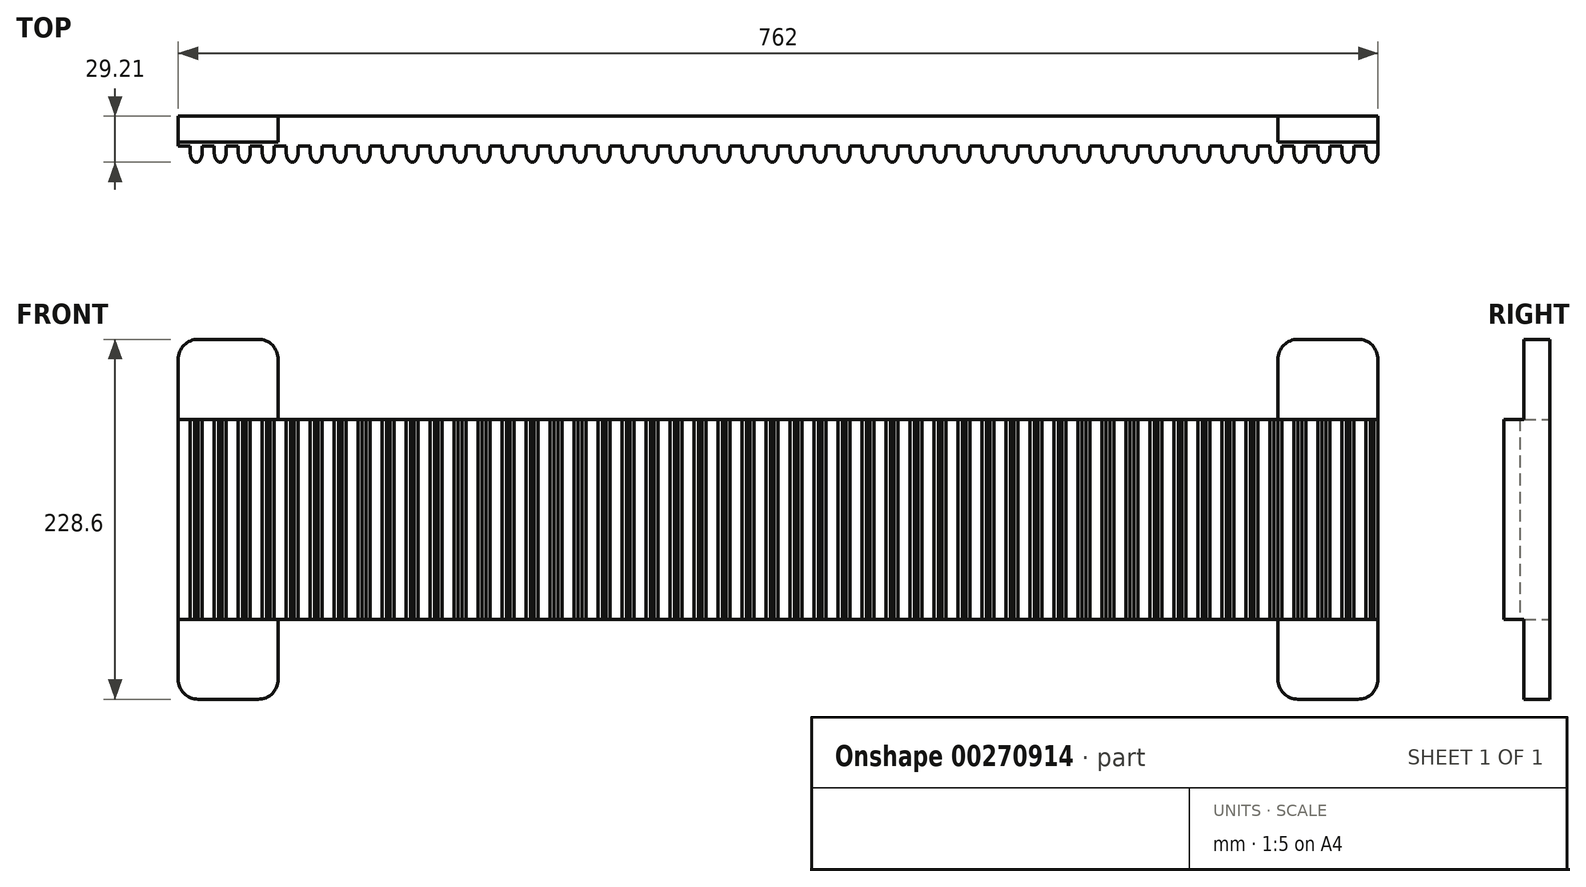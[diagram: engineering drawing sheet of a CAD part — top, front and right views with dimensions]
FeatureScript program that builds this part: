
annotation { "Feature Type Name" : "Feature", "Feature Type Description" : "" }
export const myFeature = defineFeature(function(context is Context, id is Id, definition is map)
    precondition{}
    {
        {
            var Q0;
            Q0=qCreatedBy(makeId("Front.planeOp"),FACE);
            var sketch = newSketch(context, id + "F0", { "sketchPlane" : qUnion([Q0])});
            skLineSegment(sketch, "E0", {"start": v(0, 0) * mm, "end": v(63.5, 0) * mm});
            skLineSegment(sketch, "E1.0", {"start": v(0, 228.6) * mm, "end": v(63.5, 228.6) * mm});
            skLineSegment(sketch, "E2", {"start": v(762, 0) * mm, "end": v(762, 228.6) * mm});
            skLineSegment(sketch, "E3", {"start": v(0, 228.6) * mm, "end": v(0, 0) * mm});
            skLineSegment(sketch, "E4.0", {"start": v(63.5, 177.8) * mm, "end": v(698.5, 177.8) * mm});
            skLineSegment(sketch, "E5.0", {"start": v(63.5, 50.8) * mm, "end": v(698.5, 50.8) * mm});
            skLineSegment(sketch, "E6.0", {"start": v(63.5, 228.6) * mm, "end": v(63.5, 177.8) * mm});
            skLineSegment(sketch, "E7.0", {"start": v(698.5, 0) * mm, "end": v(698.5, 50.8) * mm});
            skLineSegment(sketch, "E8.trimOffspring", {"start": v(698.5, 228.6) * mm, "end": v(762, 228.6) * mm});
            skLineSegment(sketch, "E9.trimOffspring", {"start": v(698.5, 0) * mm, "end": v(762, 0) * mm});
            skLineSegment(sketch, "E10.trimOffspring", {"start": v(698.5, 177.8) * mm, "end": v(698.5, 228.6) * mm});
            skLineSegment(sketch, "E11.trimOffspring", {"start": v(63.5, 50.8) * mm, "end": v(63.5, 0) * mm});
            skSolve(sketch);
        }
        {
            var Q0;
            Q0 = qSketchRegion(id + "F0", true);
            extrude(context, id + "F1", {"entities" : qUnion([Q0]), "depth" : 19.05 * mm});
        }
        {
            var Q0;
            Q0=makeQuery(id+"F1.opExtrude","CAP_FACE",FACE,{"disambiguationData":[OSD([sQuery(id+"F0.wireOp",EDGE,"E0"),sQuery(id+"F0.wireOp",EDGE,"E1.0"),sQuery(id+"F0.wireOp",EDGE,"E2"),sQuery(id+"F0.wireOp",EDGE,"E3"),sQuery(id+"F0.wireOp",EDGE,"E4.0"),sQuery(id+"F0.wireOp",EDGE,"E5.0"),sQuery(id+"F0.wireOp",EDGE,"E6.0"),sQuery(id+"F0.wireOp",EDGE,"E7.0"),sQuery(id+"F0.wireOp",EDGE,"E8.trimOffspring"),sQuery(id+"F0.wireOp",EDGE,"E9.trimOffspring"),sQuery(id+"F0.wireOp",EDGE,"E10.trimOffspring"),sQuery(id+"F0.wireOp",EDGE,"E11.trimOffspring")])],"isStart":false});
            var sketch = newSketch(context, id + "F2", { "sketchPlane" : qUnion([Q0])});
            skLineSegment(sketch, "E12", {"start": v(762, 177.8) * mm, "end": v(0, 177.8) * mm});
            skLineSegment(sketch, "E13", {"start": v(0, 177.8) * mm, "end": v(0, 50.8) * mm});
            skLineSegment(sketch, "E14", {"start": v(0, 50.8) * mm, "end": v(762, 50.8) * mm});
            skLineSegment(sketch, "E15", {"start": v(762, 50.8) * mm, "end": v(762, 177.8) * mm});
            skLineSegment(sketch, "E16.1.0.0", {"start": v(7.62, 177.8) * mm, "end": v(7.62, 50.8) * mm});
            skLineSegment(sketch, "E16.2.0.0", {"start": v(15.24, 177.8) * mm, "end": v(15.24, 50.8) * mm});
            skLineSegment(sketch, "E16.direction1", {"start": v(0, 50.8) * mm, "end": v(7.62, 50.8) * mm, "construction": true});
            skLineSegment(sketch, "E17.0.3.0", {"start": v(22.86, 177.8) * mm, "end": v(22.86, 50.8) * mm});
            skLineSegment(sketch, "E17.0.4.0", {"start": v(30.48, 177.8) * mm, "end": v(30.48, 50.8) * mm});
            skLineSegment(sketch, "E17.0.5.0", {"start": v(38.1, 177.8) * mm, "end": v(38.1, 50.8) * mm});
            skLineSegment(sketch, "E17.0.6.0", {"start": v(45.72, 177.8) * mm, "end": v(45.72, 50.8) * mm});
            skLineSegment(sketch, "E17.0.7.0", {"start": v(53.34, 177.8) * mm, "end": v(53.34, 50.8) * mm});
            skLineSegment(sketch, "E17.0.8.0", {"start": v(60.96, 177.8) * mm, "end": v(60.96, 50.8) * mm});
            skLineSegment(sketch, "E17.0.9.0", {"start": v(68.58, 177.8) * mm, "end": v(68.58, 50.8) * mm});
            skLineSegment(sketch, "E17.0.10.0", {"start": v(76.2, 177.8) * mm, "end": v(76.2, 50.8) * mm});
            skLineSegment(sketch, "E17.0.11.0", {"start": v(83.82, 177.8) * mm, "end": v(83.82, 50.8) * mm});
            skLineSegment(sketch, "E17.0.12.0", {"start": v(91.44, 177.8) * mm, "end": v(91.44, 50.8) * mm});
            skLineSegment(sketch, "E17.0.13.0", {"start": v(99.06, 177.8) * mm, "end": v(99.06, 50.8) * mm});
            skLineSegment(sketch, "E17.0.14.0", {"start": v(106.68, 177.8) * mm, "end": v(106.68, 50.8) * mm});
            skLineSegment(sketch, "E17.0.15.0", {"start": v(114.3, 177.8) * mm, "end": v(114.3, 50.8) * mm});
            skLineSegment(sketch, "E17.0.16.0", {"start": v(121.92, 177.8) * mm, "end": v(121.92, 50.8) * mm});
            skLineSegment(sketch, "E17.0.17.0", {"start": v(129.54, 177.8) * mm, "end": v(129.54, 50.8) * mm});
            skLineSegment(sketch, "E17.0.18.0", {"start": v(137.16, 177.8) * mm, "end": v(137.16, 50.8) * mm});
            skLineSegment(sketch, "E17.0.19.0", {"start": v(144.78, 177.8) * mm, "end": v(144.78, 50.8) * mm});
            skLineSegment(sketch, "E17.0.20.0", {"start": v(152.4, 177.8) * mm, "end": v(152.4, 50.8) * mm});
            skLineSegment(sketch, "E17.0.21.0", {"start": v(160.02, 177.8) * mm, "end": v(160.02, 50.8) * mm});
            skLineSegment(sketch, "E17.0.22.0", {"start": v(167.64, 177.8) * mm, "end": v(167.64, 50.8) * mm});
            skLineSegment(sketch, "E17.0.23.0", {"start": v(175.26, 177.8) * mm, "end": v(175.26, 50.8) * mm});
            skLineSegment(sketch, "E17.0.24.0", {"start": v(182.88, 177.8) * mm, "end": v(182.88, 50.8) * mm});
            skLineSegment(sketch, "E17.0.25.0", {"start": v(190.5, 177.8) * mm, "end": v(190.5, 50.8) * mm});
            skLineSegment(sketch, "E17.0.26.0", {"start": v(198.12, 177.8) * mm, "end": v(198.12, 50.8) * mm});
            skLineSegment(sketch, "E17.0.27.0", {"start": v(205.74, 177.8) * mm, "end": v(205.74, 50.8) * mm});
            skLineSegment(sketch, "E17.0.28.0", {"start": v(213.36, 177.8) * mm, "end": v(213.36, 50.8) * mm});
            skLineSegment(sketch, "E17.0.29.0", {"start": v(220.98, 177.8) * mm, "end": v(220.98, 50.8) * mm});
            skLineSegment(sketch, "E17.0.30.0", {"start": v(228.6, 177.8) * mm, "end": v(228.6, 50.8) * mm});
            skLineSegment(sketch, "E17.0.31.0", {"start": v(236.22, 177.8) * mm, "end": v(236.22, 50.8) * mm});
            skLineSegment(sketch, "E17.0.32.0", {"start": v(243.84, 177.8) * mm, "end": v(243.84, 50.8) * mm});
            skLineSegment(sketch, "E17.0.33.0", {"start": v(251.46, 177.8) * mm, "end": v(251.46, 50.8) * mm});
            skLineSegment(sketch, "E17.0.34.0", {"start": v(259.08, 177.8) * mm, "end": v(259.08, 50.8) * mm});
            skLineSegment(sketch, "E17.0.35.0", {"start": v(266.7, 177.8) * mm, "end": v(266.7, 50.8) * mm});
            skLineSegment(sketch, "E17.0.36.0", {"start": v(274.32, 177.8) * mm, "end": v(274.32, 50.8) * mm});
            skLineSegment(sketch, "E17.0.37.0", {"start": v(281.94, 177.8) * mm, "end": v(281.94, 50.8) * mm});
            skLineSegment(sketch, "E17.0.38.0", {"start": v(289.56, 177.8) * mm, "end": v(289.56, 50.8) * mm});
            skLineSegment(sketch, "E17.0.39.0", {"start": v(297.18, 177.8) * mm, "end": v(297.18, 50.8) * mm});
            skLineSegment(sketch, "E17.0.40.0", {"start": v(304.8, 177.8) * mm, "end": v(304.8, 50.8) * mm});
            skLineSegment(sketch, "E17.0.41.0", {"start": v(312.42, 177.8) * mm, "end": v(312.42, 50.8) * mm});
            skLineSegment(sketch, "E17.0.42.0", {"start": v(320.04, 177.8) * mm, "end": v(320.04, 50.8) * mm});
            skLineSegment(sketch, "E17.0.43.0", {"start": v(327.66, 177.8) * mm, "end": v(327.66, 50.8) * mm});
            skLineSegment(sketch, "E17.0.44.0", {"start": v(335.28, 177.8) * mm, "end": v(335.28, 50.8) * mm});
            skLineSegment(sketch, "E17.0.45.0", {"start": v(342.9, 177.8) * mm, "end": v(342.9, 50.8) * mm});
            skLineSegment(sketch, "E17.0.46.0", {"start": v(350.52, 177.8) * mm, "end": v(350.52, 50.8) * mm});
            skLineSegment(sketch, "E17.0.47.0", {"start": v(358.14, 177.8) * mm, "end": v(358.14, 50.8) * mm});
            skLineSegment(sketch, "E17.0.48.0", {"start": v(365.76, 177.8) * mm, "end": v(365.76, 50.8) * mm});
            skLineSegment(sketch, "E17.0.49.0", {"start": v(373.38, 177.8) * mm, "end": v(373.38, 50.8) * mm});
            skLineSegment(sketch, "E18.0.50.0", {"start": v(381, 177.8) * mm, "end": v(381, 50.8) * mm});
            skLineSegment(sketch, "E18.0.51.0", {"start": v(388.62, 177.8) * mm, "end": v(388.62, 50.8) * mm});
            skLineSegment(sketch, "E18.0.52.0", {"start": v(396.24, 177.8) * mm, "end": v(396.24, 50.8) * mm});
            skLineSegment(sketch, "E18.0.53.0", {"start": v(403.86, 177.8) * mm, "end": v(403.86, 50.8) * mm});
            skLineSegment(sketch, "E18.0.54.0", {"start": v(411.48, 177.8) * mm, "end": v(411.48, 50.8) * mm});
            skLineSegment(sketch, "E18.0.55.0", {"start": v(419.1, 177.8) * mm, "end": v(419.1, 50.8) * mm});
            skLineSegment(sketch, "E18.0.56.0", {"start": v(426.72, 177.8) * mm, "end": v(426.72, 50.8) * mm});
            skLineSegment(sketch, "E18.0.57.0", {"start": v(434.34, 177.8) * mm, "end": v(434.34, 50.8) * mm});
            skLineSegment(sketch, "E18.0.58.0", {"start": v(441.96, 177.8) * mm, "end": v(441.96, 50.8) * mm});
            skLineSegment(sketch, "E18.0.59.0", {"start": v(449.58, 177.8) * mm, "end": v(449.58, 50.8) * mm});
            skLineSegment(sketch, "E18.0.60.0", {"start": v(457.2, 177.8) * mm, "end": v(457.2, 50.8) * mm});
            skLineSegment(sketch, "E18.0.61.0", {"start": v(464.82, 177.8) * mm, "end": v(464.82, 50.8) * mm});
            skLineSegment(sketch, "E18.0.62.0", {"start": v(472.44, 177.8) * mm, "end": v(472.44, 50.8) * mm});
            skLineSegment(sketch, "E18.0.63.0", {"start": v(480.06, 177.8) * mm, "end": v(480.06, 50.8) * mm});
            skLineSegment(sketch, "E18.0.64.0", {"start": v(487.68, 177.8) * mm, "end": v(487.68, 50.8) * mm});
            skLineSegment(sketch, "E18.0.65.0", {"start": v(495.3, 177.8) * mm, "end": v(495.3, 50.8) * mm});
            skLineSegment(sketch, "E18.0.66.0", {"start": v(502.92, 177.8) * mm, "end": v(502.92, 50.8) * mm});
            skLineSegment(sketch, "E18.0.67.0", {"start": v(510.54, 177.8) * mm, "end": v(510.54, 50.8) * mm});
            skLineSegment(sketch, "E18.0.68.0", {"start": v(518.16, 177.8) * mm, "end": v(518.16, 50.8) * mm});
            skLineSegment(sketch, "E18.0.69.0", {"start": v(525.78, 177.8) * mm, "end": v(525.78, 50.8) * mm});
            skLineSegment(sketch, "E18.0.70.0", {"start": v(533.4, 177.8) * mm, "end": v(533.4, 50.8) * mm});
            skLineSegment(sketch, "E18.0.71.0", {"start": v(541.02, 177.8) * mm, "end": v(541.02, 50.8) * mm});
            skLineSegment(sketch, "E18.0.72.0", {"start": v(548.64, 177.8) * mm, "end": v(548.64, 50.8) * mm});
            skLineSegment(sketch, "E18.0.73.0", {"start": v(556.26, 177.8) * mm, "end": v(556.26, 50.8) * mm});
            skLineSegment(sketch, "E18.0.74.0", {"start": v(563.88, 177.8) * mm, "end": v(563.88, 50.8) * mm});
            skLineSegment(sketch, "E18.0.75.0", {"start": v(571.5, 177.8) * mm, "end": v(571.5, 50.8) * mm});
            skLineSegment(sketch, "E18.0.76.0", {"start": v(579.12, 177.8) * mm, "end": v(579.12, 50.8) * mm});
            skLineSegment(sketch, "E18.0.77.0", {"start": v(586.74, 177.8) * mm, "end": v(586.74, 50.8) * mm});
            skLineSegment(sketch, "E18.0.78.0", {"start": v(594.36, 177.8) * mm, "end": v(594.36, 50.8) * mm});
            skLineSegment(sketch, "E18.0.79.0", {"start": v(601.98, 177.8) * mm, "end": v(601.98, 50.8) * mm});
            skLineSegment(sketch, "E18.0.80.0", {"start": v(609.6, 177.8) * mm, "end": v(609.6, 50.8) * mm});
            skLineSegment(sketch, "E18.0.81.0", {"start": v(617.22, 177.8) * mm, "end": v(617.22, 50.8) * mm});
            skLineSegment(sketch, "E18.0.82.0", {"start": v(624.84, 177.8) * mm, "end": v(624.84, 50.8) * mm});
            skLineSegment(sketch, "E18.0.83.0", {"start": v(632.46, 177.8) * mm, "end": v(632.46, 50.8) * mm});
            skLineSegment(sketch, "E18.0.84.0", {"start": v(640.08, 177.8) * mm, "end": v(640.08, 50.8) * mm});
            skLineSegment(sketch, "E18.0.85.0", {"start": v(647.7, 177.8) * mm, "end": v(647.7, 50.8) * mm});
            skLineSegment(sketch, "E18.0.86.0", {"start": v(655.32, 177.8) * mm, "end": v(655.32, 50.8) * mm});
            skLineSegment(sketch, "E18.0.87.0", {"start": v(662.94, 177.8) * mm, "end": v(662.94, 50.8) * mm});
            skLineSegment(sketch, "E18.0.88.0", {"start": v(670.56, 177.8) * mm, "end": v(670.56, 50.8) * mm});
            skLineSegment(sketch, "E18.0.89.0", {"start": v(678.18, 177.8) * mm, "end": v(678.18, 50.8) * mm});
            skLineSegment(sketch, "E18.0.90.0", {"start": v(685.8, 177.8) * mm, "end": v(685.8, 50.8) * mm});
            skLineSegment(sketch, "E18.0.91.0", {"start": v(693.42, 177.8) * mm, "end": v(693.42, 50.8) * mm});
            skLineSegment(sketch, "E18.0.92.0", {"start": v(701.04, 177.8) * mm, "end": v(701.04, 50.8) * mm});
            skLineSegment(sketch, "E18.0.93.0", {"start": v(708.66, 177.8) * mm, "end": v(708.66, 50.8) * mm});
            skLineSegment(sketch, "E18.0.94.0", {"start": v(716.28, 177.8) * mm, "end": v(716.28, 50.8) * mm});
            skLineSegment(sketch, "E18.0.95.0", {"start": v(723.9, 177.8) * mm, "end": v(723.9, 50.8) * mm});
            skLineSegment(sketch, "E18.0.96.0", {"start": v(731.52, 177.8) * mm, "end": v(731.52, 50.8) * mm});
            skLineSegment(sketch, "E18.0.97.0", {"start": v(739.14, 177.8) * mm, "end": v(739.14, 50.8) * mm});
            skLineSegment(sketch, "E18.0.98.0", {"start": v(746.76, 177.8) * mm, "end": v(746.76, 50.8) * mm});
            skLineSegment(sketch, "E18.0.99.0", {"start": v(754.38, 177.8) * mm, "end": v(754.38, 50.8) * mm});
            skSolve(sketch);
        }
        {
            var Q0;
            {var subQ7=makeQuery(id+"F1.opExtrude","CAP_EDGE",EDGE,{"disambiguationData":[OSD([sQuery(id+"F0.wireOp",EDGE,"E1.0")])],"isStart":false});Q0=makeQuery(id+"F2.imprint","IMPRINT",FACE,{"disambiguationData":[TD([[makeQuery(id+"F2.imprint","IMPRINT",EDGE,{"derivedFrom":subQ7}),-1.0]])]});}
            var sketch = newSketch(context, id + "F3", { "sketchPlane" : qUnion([Q0])});
            skLineSegment(sketch, "E19", {"start": v(0, 228.6) * mm, "end": v(63.5, 228.6) * mm});
            skLineSegment(sketch, "E20", {"start": v(63.5, 228.6) * mm, "end": v(63.5, 177.8) * mm});
            skLineSegment(sketch, "E21", {"start": v(63.5, 177.8) * mm, "end": v(0, 177.8) * mm});
            skLineSegment(sketch, "E22", {"start": v(0, 0) * mm, "end": v(0, 50.8) * mm});
            skLineSegment(sketch, "E23", {"start": v(0, 50.8) * mm, "end": v(63.5, 50.8) * mm});
            skLineSegment(sketch, "E24", {"start": v(63.5, 50.8) * mm, "end": v(63.5, 0) * mm});
            skLineSegment(sketch, "E25", {"start": v(63.5, 0) * mm, "end": v(0, 0) * mm});
            skSolve(sketch);
        }
        {
            var Q0;
            Q0 = qSketchRegion(id + "F3", true);
            var Q1;
            {var subQ8=sQuery(id+"F3.wireOp",EDGE,"E19");Q1=makeQuery(id+"F3.imprint","IMPRINT",FACE,{"disambiguationData":[TD([[makeQuery(id+"F3.imprint","IMPRINT",EDGE,{"derivedFrom":subQ8}),-1.0]])]});}
            extrude(context, id + "F4", {"entities" : qUnion([Q0, Q1]), "operationType" : NewBodyOperationType.REMOVE, "oppositeDirection" : true, "depth" : 2.54 * mm});
        }
        {
            var Q0;
            {var subQ1=sQuery(id+"F0.wireOp",EDGE,"E7.0");var subQ7=sQuery(id+"F0.wireOp",EDGE,"E8.trimOffspring");var subQ10=sQuery(id+"F0.wireOp",EDGE,"E9.trimOffspring");var subQ50=sQuery(id+"F0.wireOp",EDGE,"E4.0");var subQ83=sQuery(id+"F0.wireOp",EDGE,"E10.trimOffspring");var subQ89=sQuery(id+"F0.wireOp",EDGE,"E2");var subQ94=sQuery(id+"F0.wireOp",EDGE,"E5.0");Q0=makeQuery(id+"F9L2YdqkWQCteiL_1.boolean.opBoolean","SPLIT",FACE,{"disambiguationData":[TD([makeQuery(id+"F1.opExtrude","SWEPT_FACE",FACE,{"disambiguationData":[OSD([subQ89])]})])],"derivedFrom":makeQuery(id+"F1.opExtrude","CAP_FACE",FACE,{"disambiguationData":[OSD([sQuery(id+"F0.wireOp",EDGE,"E0"),sQuery(id+"F0.wireOp",EDGE,"E1.0"),subQ89,sQuery(id+"F0.wireOp",EDGE,"E3"),subQ50,subQ94,sQuery(id+"F0.wireOp",EDGE,"E6.0"),subQ1,subQ7,subQ10,subQ83,sQuery(id+"F0.wireOp",EDGE,"E11.trimOffspring")])],"isStart":false})});}
            var sketch = newSketch(context, id + "F5", { "sketchPlane" : qUnion([Q0])});
            skLineSegment(sketch, "E26", {"start": v(698.5, 228.6) * mm, "end": v(698.5, 177.8) * mm});
            skLineSegment(sketch, "E27", {"start": v(698.5, 177.8) * mm, "end": v(762, 177.8) * mm});
            skLineSegment(sketch, "E28", {"start": v(762, 177.8) * mm, "end": v(762, 228.6) * mm});
            skLineSegment(sketch, "E29", {"start": v(762, 228.6) * mm, "end": v(698.5, 228.6) * mm});
            skLineSegment(sketch, "E30", {"start": v(698.5, 0) * mm, "end": v(762, 0) * mm});
            skLineSegment(sketch, "E31", {"start": v(762, 0) * mm, "end": v(762, 50.8) * mm});
            skLineSegment(sketch, "E32", {"start": v(762, 50.8) * mm, "end": v(701.04, 50.8) * mm});
            skLineSegment(sketch, "E33", {"start": v(701.04, 50.8) * mm, "end": v(698.5, 50.8) * mm});
            skLineSegment(sketch, "E34", {"start": v(698.5, 50.8) * mm, "end": v(698.5, 0) * mm});
            skSolve(sketch);
        }
        {
            var Q0;
            {var subQ7=sQuery(id+"F5.wireOp",EDGE,"E26");Q0=makeQuery(id+"F5.imprint","IMPRINT",FACE,{"disambiguationData":[TD([[makeQuery(id+"F5.imprint","IMPRINT",EDGE,{"derivedFrom":subQ7}),-1.0]])]});}
            var Q1;
            Q1=makeQuery(id+"F5.imprint","IMPRINT",FACE,{"disambiguationData":[TD([[makeQuery(id+"F5.imprint","IMPRINT",EDGE,{"derivedFrom":sQuery(id+"F5.wireOp",EDGE,"E30")}),1.0]])]});
            extrude(context, id + "F6", {"entities" : qUnion([Q0, Q1]), "operationType" : NewBodyOperationType.REMOVE, "oppositeDirection" : true, "depth" : 2.54 * mm});
        }
        {
            var Q0;
            Q0=makeQuery(id+"F1.opExtrude","SWEPT_EDGE",EDGE,{"disambiguationData":[OSD([sQuery(id+"F0.wireOp",EDGE,"E1.0"),sQuery(id+"F0.wireOp",EDGE,"E6.0")])]});
            var Q1;
            Q1=makeQuery(id+"F1.opExtrude","SWEPT_EDGE",EDGE,{"disambiguationData":[OSD([sQuery(id+"F0.wireOp",EDGE,"E1.0"),sQuery(id+"F0.wireOp",EDGE,"E3")])]});
            var Q2;
            Q2=makeQuery(id+"F1.opExtrude","SWEPT_EDGE",EDGE,{"disambiguationData":[OSD([sQuery(id+"F0.wireOp",EDGE,"E0"),sQuery(id+"F0.wireOp",EDGE,"E11.trimOffspring")])]});
            var Q3;
            Q3=makeQuery(id+"F1.opExtrude","SWEPT_EDGE",EDGE,{"disambiguationData":[OSD([sQuery(id+"F0.wireOp",EDGE,"E0"),sQuery(id+"F0.wireOp",EDGE,"E3")])]});
            var Q4;
            Q4=makeQuery(id+"F1.opExtrude","SWEPT_EDGE",EDGE,{"disambiguationData":[OSD([sQuery(id+"F0.wireOp",EDGE,"E2"),sQuery(id+"F0.wireOp",EDGE,"E8.trimOffspring")])]});
            var Q5;
            Q5=makeQuery(id+"F1.opExtrude","SWEPT_EDGE",EDGE,{"disambiguationData":[OSD([sQuery(id+"F0.wireOp",EDGE,"E8.trimOffspring"),sQuery(id+"F0.wireOp",EDGE,"E10.trimOffspring")])]});
            var Q6;
            Q6=makeQuery(id+"F1.opExtrude","SWEPT_EDGE",EDGE,{"disambiguationData":[OSD([sQuery(id+"F0.wireOp",EDGE,"E2"),sQuery(id+"F0.wireOp",EDGE,"E9.trimOffspring")])]});
            var Q7;
            Q7=makeQuery(id+"F1.opExtrude","SWEPT_EDGE",EDGE,{"disambiguationData":[OSD([sQuery(id+"F0.wireOp",EDGE,"E7.0"),sQuery(id+"F0.wireOp",EDGE,"E9.trimOffspring")])]});
            fillet(context, id + "F7", {"entities" : qUnion([Q0, Q1, Q2, Q3, Q4, Q5, Q6, Q7]), "radius" : 12.7 * mm, "tangentPropagation" : true, "allowEdgeOverflow" : false});
        }
        {
            var Q0;
            {var subQ0=sQuery(id+"F2.wireOp",EDGE,"E14");var subQ1=makeQuery(id+"F2.imprint","INTERSECT",VERTEX,{"derivedFrom":[makeQuery(id+"F1.opExtrude","CAP_EDGE",EDGE,{"disambiguationData":[OSD([sQuery(id+"F0.wireOp",EDGE,"E7.0")])],"isStart":false}),subQ0]});Q0=makeQuery(id+"F6.boolean.opBoolean","MERGE",FACE,{"derivedFrom":[makeQuery(id+"F9L2YdqkWQCteiL_1.opExtrude","SWEPT_FACE",FACE,{"disambiguationData":[OSD([subQ0]),TDD([makeQuery(id+"F2.imprint","IMPRINT",EDGE,{"disambiguationData":[TD([[makeQuery(id+"F2.imprint","INTERSECT",VERTEX,{"derivedFrom":[subQ0,sQuery(id+"F2.wireOp",EDGE,"E18.0.93.0")]}),-1.0]])],"derivedFrom":subQ0})])]}),makeQuery(id+"F9L2YdqkWQCteiL_1.opExtrude","SWEPT_FACE",FACE,{"disambiguationData":[OSD([subQ0]),TDD([makeQuery(id+"F2.imprint","IMPRINT",EDGE,{"disambiguationData":[TD([[makeQuery(id+"F2.imprint","INTERSECT",VERTEX,{"derivedFrom":[subQ0,sQuery(id+"F2.wireOp",EDGE,"E18.0.95.0")]}),-1.0]])],"derivedFrom":subQ0})])]}),makeQuery(id+"F9L2YdqkWQCteiL_1.opExtrude","SWEPT_FACE",FACE,{"disambiguationData":[OSD([subQ0]),TDD([makeQuery(id+"F2.imprint","IMPRINT",EDGE,{"disambiguationData":[TD([[makeQuery(id+"F2.imprint","INTERSECT",VERTEX,{"derivedFrom":[subQ0,sQuery(id+"F2.wireOp",EDGE,"E18.0.97.0")]}),-1.0]])],"derivedFrom":subQ0})])]}),makeQuery(id+"F9L2YdqkWQCteiL_1.opExtrude","SWEPT_FACE",FACE,{"disambiguationData":[OSD([subQ0]),TDD([makeQuery(id+"F2.imprint","IMPRINT",EDGE,{"disambiguationData":[TD([[makeQuery(id+"F2.imprint","INTERSECT",VERTEX,{"derivedFrom":[subQ0,sQuery(id+"F2.wireOp",EDGE,"E18.0.99.0")]}),-1.0]])],"derivedFrom":subQ0})])]}),makeQuery(id+"F4.boolean.opBoolean","MERGE",FACE,{"derivedFrom":[makeQuery(id+"F9L2YdqkWQCteiL_1.opExtrude","SWEPT_FACE",FACE,{"disambiguationData":[OSD([subQ0]),TDD([makeQuery(id+"F2.imprint","IMPRINT",EDGE,{"disambiguationData":[TD([[makeQuery(id+"F2.imprint","INTERSECT",VERTEX,{"derivedFrom":[subQ0,sQuery(id+"F2.wireOp",EDGE,"E16.1.0.0")]}),-1.0]])],"derivedFrom":subQ0})])]}),makeQuery(id+"F9L2YdqkWQCteiL_1.opExtrude","SWEPT_FACE",FACE,{"disambiguationData":[OSD([subQ0]),TDD([makeQuery(id+"F2.imprint","IMPRINT",EDGE,{"disambiguationData":[TD([[makeQuery(id+"F2.imprint","INTERSECT",VERTEX,{"derivedFrom":[subQ0,sQuery(id+"F2.wireOp",EDGE,"E17.0.3.0")]}),-1.0]])],"derivedFrom":subQ0})])]}),makeQuery(id+"F9L2YdqkWQCteiL_1.opExtrude","SWEPT_FACE",FACE,{"disambiguationData":[OSD([subQ0]),TDD([makeQuery(id+"F2.imprint","IMPRINT",EDGE,{"disambiguationData":[TD([[makeQuery(id+"F2.imprint","INTERSECT",VERTEX,{"derivedFrom":[subQ0,sQuery(id+"F2.wireOp",EDGE,"E17.0.5.0")]}),-1.0]])],"derivedFrom":subQ0})])]}),makeQuery(id+"F9L2YdqkWQCteiL_1.opExtrude","SWEPT_FACE",FACE,{"disambiguationData":[OSD([subQ0]),TDD([makeQuery(id+"F2.imprint","IMPRINT",EDGE,{"disambiguationData":[TD([[makeQuery(id+"F2.imprint","INTERSECT",VERTEX,{"derivedFrom":[subQ0,sQuery(id+"F2.wireOp",EDGE,"E17.0.7.0")]}),-1.0]])],"derivedFrom":subQ0})])]}),makeQuery(id+"F9L2YdqkWQCteiL_1.boolean.opBoolean","MERGE",FACE,{"derivedFrom":[makeQuery(id+"F1.opExtrude","SWEPT_FACE",FACE,{"disambiguationData":[OSD([sQuery(id+"F0.wireOp",EDGE,"E5.0")])]}),makeQuery(id+"F9L2YdqkWQCteiL_1.opExtrude","SWEPT_FACE",FACE,{"disambiguationData":[OSD([subQ0]),TDD([makeQuery(id+"F2.imprint","IMPRINT",EDGE,{"disambiguationData":[TD([[makeQuery(id+"F2.imprint","INTERSECT",VERTEX,{"derivedFrom":[subQ0,sQuery(id+"F2.wireOp",EDGE,"E17.0.9.0")]}),-1.0]])],"derivedFrom":subQ0})])]}),makeQuery(id+"F9L2YdqkWQCteiL_1.opExtrude","SWEPT_FACE",FACE,{"disambiguationData":[OSD([subQ0]),TDD([makeQuery(id+"F2.imprint","IMPRINT",EDGE,{"disambiguationData":[TD([[makeQuery(id+"F2.imprint","INTERSECT",VERTEX,{"derivedFrom":[subQ0,sQuery(id+"F2.wireOp",EDGE,"E17.0.11.0")]}),-1.0]])],"derivedFrom":subQ0})])]}),makeQuery(id+"F9L2YdqkWQCteiL_1.opExtrude","SWEPT_FACE",FACE,{"disambiguationData":[OSD([subQ0]),TDD([makeQuery(id+"F2.imprint","IMPRINT",EDGE,{"disambiguationData":[TD([[makeQuery(id+"F2.imprint","INTERSECT",VERTEX,{"derivedFrom":[subQ0,sQuery(id+"F2.wireOp",EDGE,"E17.0.13.0")]}),-1.0]])],"derivedFrom":subQ0})])]}),makeQuery(id+"F9L2YdqkWQCteiL_1.opExtrude","SWEPT_FACE",FACE,{"disambiguationData":[OSD([subQ0]),TDD([makeQuery(id+"F2.imprint","IMPRINT",EDGE,{"disambiguationData":[TD([[makeQuery(id+"F2.imprint","INTERSECT",VERTEX,{"derivedFrom":[subQ0,sQuery(id+"F2.wireOp",EDGE,"E17.0.15.0")]}),-1.0]])],"derivedFrom":subQ0})])]}),makeQuery(id+"F9L2YdqkWQCteiL_1.opExtrude","SWEPT_FACE",FACE,{"disambiguationData":[OSD([subQ0]),TDD([makeQuery(id+"F2.imprint","IMPRINT",EDGE,{"disambiguationData":[TD([[makeQuery(id+"F2.imprint","INTERSECT",VERTEX,{"derivedFrom":[subQ0,sQuery(id+"F2.wireOp",EDGE,"E17.0.17.0")]}),-1.0]])],"derivedFrom":subQ0})])]}),makeQuery(id+"F9L2YdqkWQCteiL_1.opExtrude","SWEPT_FACE",FACE,{"disambiguationData":[OSD([subQ0]),TDD([makeQuery(id+"F2.imprint","IMPRINT",EDGE,{"disambiguationData":[TD([[makeQuery(id+"F2.imprint","INTERSECT",VERTEX,{"derivedFrom":[subQ0,sQuery(id+"F2.wireOp",EDGE,"E17.0.19.0")]}),-1.0]])],"derivedFrom":subQ0})])]}),makeQuery(id+"F9L2YdqkWQCteiL_1.opExtrude","SWEPT_FACE",FACE,{"disambiguationData":[OSD([subQ0]),TDD([makeQuery(id+"F2.imprint","IMPRINT",EDGE,{"disambiguationData":[TD([[makeQuery(id+"F2.imprint","INTERSECT",VERTEX,{"derivedFrom":[subQ0,sQuery(id+"F2.wireOp",EDGE,"E17.0.21.0")]}),-1.0]])],"derivedFrom":subQ0})])]}),makeQuery(id+"F9L2YdqkWQCteiL_1.opExtrude","SWEPT_FACE",FACE,{"disambiguationData":[OSD([subQ0]),TDD([makeQuery(id+"F2.imprint","IMPRINT",EDGE,{"disambiguationData":[TD([[makeQuery(id+"F2.imprint","INTERSECT",VERTEX,{"derivedFrom":[subQ0,sQuery(id+"F2.wireOp",EDGE,"E17.0.23.0")]}),-1.0]])],"derivedFrom":subQ0})])]}),makeQuery(id+"F9L2YdqkWQCteiL_1.opExtrude","SWEPT_FACE",FACE,{"disambiguationData":[OSD([subQ0]),TDD([makeQuery(id+"F2.imprint","IMPRINT",EDGE,{"disambiguationData":[TD([[makeQuery(id+"F2.imprint","INTERSECT",VERTEX,{"derivedFrom":[subQ0,sQuery(id+"F2.wireOp",EDGE,"E17.0.25.0")]}),-1.0]])],"derivedFrom":subQ0})])]}),makeQuery(id+"F9L2YdqkWQCteiL_1.opExtrude","SWEPT_FACE",FACE,{"disambiguationData":[OSD([subQ0]),TDD([makeQuery(id+"F2.imprint","IMPRINT",EDGE,{"disambiguationData":[TD([[makeQuery(id+"F2.imprint","INTERSECT",VERTEX,{"derivedFrom":[subQ0,sQuery(id+"F2.wireOp",EDGE,"E17.0.27.0")]}),-1.0]])],"derivedFrom":subQ0})])]}),makeQuery(id+"F9L2YdqkWQCteiL_1.opExtrude","SWEPT_FACE",FACE,{"disambiguationData":[OSD([subQ0]),TDD([makeQuery(id+"F2.imprint","IMPRINT",EDGE,{"disambiguationData":[TD([[makeQuery(id+"F2.imprint","INTERSECT",VERTEX,{"derivedFrom":[subQ0,sQuery(id+"F2.wireOp",EDGE,"E17.0.29.0")]}),-1.0]])],"derivedFrom":subQ0})])]}),makeQuery(id+"F9L2YdqkWQCteiL_1.opExtrude","SWEPT_FACE",FACE,{"disambiguationData":[OSD([subQ0]),TDD([makeQuery(id+"F2.imprint","IMPRINT",EDGE,{"disambiguationData":[TD([[makeQuery(id+"F2.imprint","INTERSECT",VERTEX,{"derivedFrom":[subQ0,sQuery(id+"F2.wireOp",EDGE,"E17.0.31.0")]}),-1.0]])],"derivedFrom":subQ0})])]}),makeQuery(id+"F9L2YdqkWQCteiL_1.opExtrude","SWEPT_FACE",FACE,{"disambiguationData":[OSD([subQ0]),TDD([makeQuery(id+"F2.imprint","IMPRINT",EDGE,{"disambiguationData":[TD([[makeQuery(id+"F2.imprint","INTERSECT",VERTEX,{"derivedFrom":[subQ0,sQuery(id+"F2.wireOp",EDGE,"E17.0.33.0")]}),-1.0]])],"derivedFrom":subQ0})])]}),makeQuery(id+"F9L2YdqkWQCteiL_1.opExtrude","SWEPT_FACE",FACE,{"disambiguationData":[OSD([subQ0]),TDD([makeQuery(id+"F2.imprint","IMPRINT",EDGE,{"disambiguationData":[TD([[makeQuery(id+"F2.imprint","INTERSECT",VERTEX,{"derivedFrom":[subQ0,sQuery(id+"F2.wireOp",EDGE,"E17.0.35.0")]}),-1.0]])],"derivedFrom":subQ0})])]}),makeQuery(id+"F9L2YdqkWQCteiL_1.opExtrude","SWEPT_FACE",FACE,{"disambiguationData":[OSD([subQ0]),TDD([makeQuery(id+"F2.imprint","IMPRINT",EDGE,{"disambiguationData":[TD([[makeQuery(id+"F2.imprint","INTERSECT",VERTEX,{"derivedFrom":[subQ0,sQuery(id+"F2.wireOp",EDGE,"E17.0.37.0")]}),-1.0]])],"derivedFrom":subQ0})])]}),makeQuery(id+"F9L2YdqkWQCteiL_1.opExtrude","SWEPT_FACE",FACE,{"disambiguationData":[OSD([subQ0]),TDD([makeQuery(id+"F2.imprint","IMPRINT",EDGE,{"disambiguationData":[TD([[makeQuery(id+"F2.imprint","INTERSECT",VERTEX,{"derivedFrom":[subQ0,sQuery(id+"F2.wireOp",EDGE,"E17.0.39.0")]}),-1.0]])],"derivedFrom":subQ0})])]}),makeQuery(id+"F9L2YdqkWQCteiL_1.opExtrude","SWEPT_FACE",FACE,{"disambiguationData":[OSD([subQ0]),TDD([makeQuery(id+"F2.imprint","IMPRINT",EDGE,{"disambiguationData":[TD([[makeQuery(id+"F2.imprint","INTERSECT",VERTEX,{"derivedFrom":[subQ0,sQuery(id+"F2.wireOp",EDGE,"E17.0.41.0")]}),-1.0]])],"derivedFrom":subQ0})])]}),makeQuery(id+"F9L2YdqkWQCteiL_1.opExtrude","SWEPT_FACE",FACE,{"disambiguationData":[OSD([subQ0]),TDD([makeQuery(id+"F2.imprint","IMPRINT",EDGE,{"disambiguationData":[TD([[makeQuery(id+"F2.imprint","INTERSECT",VERTEX,{"derivedFrom":[subQ0,sQuery(id+"F2.wireOp",EDGE,"E17.0.43.0")]}),-1.0]])],"derivedFrom":subQ0})])]}),makeQuery(id+"F9L2YdqkWQCteiL_1.opExtrude","SWEPT_FACE",FACE,{"disambiguationData":[OSD([subQ0]),TDD([makeQuery(id+"F2.imprint","IMPRINT",EDGE,{"disambiguationData":[TD([[makeQuery(id+"F2.imprint","INTERSECT",VERTEX,{"derivedFrom":[subQ0,sQuery(id+"F2.wireOp",EDGE,"E17.0.45.0")]}),-1.0]])],"derivedFrom":subQ0})])]}),makeQuery(id+"F9L2YdqkWQCteiL_1.opExtrude","SWEPT_FACE",FACE,{"disambiguationData":[OSD([subQ0]),TDD([makeQuery(id+"F2.imprint","IMPRINT",EDGE,{"disambiguationData":[TD([[makeQuery(id+"F2.imprint","INTERSECT",VERTEX,{"derivedFrom":[subQ0,sQuery(id+"F2.wireOp",EDGE,"E17.0.47.0")]}),-1.0]])],"derivedFrom":subQ0})])]}),makeQuery(id+"F9L2YdqkWQCteiL_1.opExtrude","SWEPT_FACE",FACE,{"disambiguationData":[OSD([subQ0]),TDD([makeQuery(id+"F2.imprint","IMPRINT",EDGE,{"disambiguationData":[TD([[makeQuery(id+"F2.imprint","INTERSECT",VERTEX,{"derivedFrom":[subQ0,sQuery(id+"F2.wireOp",EDGE,"E17.0.49.0")]}),-1.0]])],"derivedFrom":subQ0})])]}),makeQuery(id+"F9L2YdqkWQCteiL_1.opExtrude","SWEPT_FACE",FACE,{"disambiguationData":[OSD([subQ0]),TDD([makeQuery(id+"F2.imprint","IMPRINT",EDGE,{"disambiguationData":[TD([[makeQuery(id+"F2.imprint","INTERSECT",VERTEX,{"derivedFrom":[subQ0,sQuery(id+"F2.wireOp",EDGE,"E18.0.51.0")]}),-1.0]])],"derivedFrom":subQ0})])]}),makeQuery(id+"F9L2YdqkWQCteiL_1.opExtrude","SWEPT_FACE",FACE,{"disambiguationData":[OSD([subQ0]),TDD([makeQuery(id+"F2.imprint","IMPRINT",EDGE,{"disambiguationData":[TD([[makeQuery(id+"F2.imprint","INTERSECT",VERTEX,{"derivedFrom":[subQ0,sQuery(id+"F2.wireOp",EDGE,"E18.0.53.0")]}),-1.0]])],"derivedFrom":subQ0})])]}),makeQuery(id+"F9L2YdqkWQCteiL_1.opExtrude","SWEPT_FACE",FACE,{"disambiguationData":[OSD([subQ0]),TDD([makeQuery(id+"F2.imprint","IMPRINT",EDGE,{"disambiguationData":[TD([[makeQuery(id+"F2.imprint","INTERSECT",VERTEX,{"derivedFrom":[subQ0,sQuery(id+"F2.wireOp",EDGE,"E18.0.55.0")]}),-1.0]])],"derivedFrom":subQ0})])]}),makeQuery(id+"F9L2YdqkWQCteiL_1.opExtrude","SWEPT_FACE",FACE,{"disambiguationData":[OSD([subQ0]),TDD([makeQuery(id+"F2.imprint","IMPRINT",EDGE,{"disambiguationData":[TD([[makeQuery(id+"F2.imprint","INTERSECT",VERTEX,{"derivedFrom":[subQ0,sQuery(id+"F2.wireOp",EDGE,"E18.0.57.0")]}),-1.0]])],"derivedFrom":subQ0})])]}),makeQuery(id+"F9L2YdqkWQCteiL_1.opExtrude","SWEPT_FACE",FACE,{"disambiguationData":[OSD([subQ0]),TDD([makeQuery(id+"F2.imprint","IMPRINT",EDGE,{"disambiguationData":[TD([[makeQuery(id+"F2.imprint","INTERSECT",VERTEX,{"derivedFrom":[subQ0,sQuery(id+"F2.wireOp",EDGE,"E18.0.59.0")]}),-1.0]])],"derivedFrom":subQ0})])]}),makeQuery(id+"F9L2YdqkWQCteiL_1.opExtrude","SWEPT_FACE",FACE,{"disambiguationData":[OSD([subQ0]),TDD([makeQuery(id+"F2.imprint","IMPRINT",EDGE,{"disambiguationData":[TD([[makeQuery(id+"F2.imprint","INTERSECT",VERTEX,{"derivedFrom":[subQ0,sQuery(id+"F2.wireOp",EDGE,"E18.0.61.0")]}),-1.0]])],"derivedFrom":subQ0})])]}),makeQuery(id+"F9L2YdqkWQCteiL_1.opExtrude","SWEPT_FACE",FACE,{"disambiguationData":[OSD([subQ0]),TDD([makeQuery(id+"F2.imprint","IMPRINT",EDGE,{"disambiguationData":[TD([[makeQuery(id+"F2.imprint","INTERSECT",VERTEX,{"derivedFrom":[subQ0,sQuery(id+"F2.wireOp",EDGE,"E18.0.63.0")]}),-1.0]])],"derivedFrom":subQ0})])]}),makeQuery(id+"F9L2YdqkWQCteiL_1.opExtrude","SWEPT_FACE",FACE,{"disambiguationData":[OSD([subQ0]),TDD([makeQuery(id+"F2.imprint","IMPRINT",EDGE,{"disambiguationData":[TD([[makeQuery(id+"F2.imprint","INTERSECT",VERTEX,{"derivedFrom":[subQ0,sQuery(id+"F2.wireOp",EDGE,"E18.0.65.0")]}),-1.0]])],"derivedFrom":subQ0})])]}),makeQuery(id+"F9L2YdqkWQCteiL_1.opExtrude","SWEPT_FACE",FACE,{"disambiguationData":[OSD([subQ0]),TDD([makeQuery(id+"F2.imprint","IMPRINT",EDGE,{"disambiguationData":[TD([[makeQuery(id+"F2.imprint","INTERSECT",VERTEX,{"derivedFrom":[subQ0,sQuery(id+"F2.wireOp",EDGE,"E18.0.67.0")]}),-1.0]])],"derivedFrom":subQ0})])]}),makeQuery(id+"F9L2YdqkWQCteiL_1.opExtrude","SWEPT_FACE",FACE,{"disambiguationData":[OSD([subQ0]),TDD([makeQuery(id+"F2.imprint","IMPRINT",EDGE,{"disambiguationData":[TD([[makeQuery(id+"F2.imprint","INTERSECT",VERTEX,{"derivedFrom":[subQ0,sQuery(id+"F2.wireOp",EDGE,"E18.0.69.0")]}),-1.0]])],"derivedFrom":subQ0})])]}),makeQuery(id+"F9L2YdqkWQCteiL_1.opExtrude","SWEPT_FACE",FACE,{"disambiguationData":[OSD([subQ0]),TDD([makeQuery(id+"F2.imprint","IMPRINT",EDGE,{"disambiguationData":[TD([[makeQuery(id+"F2.imprint","INTERSECT",VERTEX,{"derivedFrom":[subQ0,sQuery(id+"F2.wireOp",EDGE,"E18.0.71.0")]}),-1.0]])],"derivedFrom":subQ0})])]}),makeQuery(id+"F9L2YdqkWQCteiL_1.opExtrude","SWEPT_FACE",FACE,{"disambiguationData":[OSD([subQ0]),TDD([makeQuery(id+"F2.imprint","IMPRINT",EDGE,{"disambiguationData":[TD([[makeQuery(id+"F2.imprint","INTERSECT",VERTEX,{"derivedFrom":[subQ0,sQuery(id+"F2.wireOp",EDGE,"E18.0.73.0")]}),-1.0]])],"derivedFrom":subQ0})])]}),makeQuery(id+"F9L2YdqkWQCteiL_1.opExtrude","SWEPT_FACE",FACE,{"disambiguationData":[OSD([subQ0]),TDD([makeQuery(id+"F2.imprint","IMPRINT",EDGE,{"disambiguationData":[TD([[makeQuery(id+"F2.imprint","INTERSECT",VERTEX,{"derivedFrom":[subQ0,sQuery(id+"F2.wireOp",EDGE,"E18.0.75.0")]}),-1.0]])],"derivedFrom":subQ0})])]}),makeQuery(id+"F9L2YdqkWQCteiL_1.opExtrude","SWEPT_FACE",FACE,{"disambiguationData":[OSD([subQ0]),TDD([makeQuery(id+"F2.imprint","IMPRINT",EDGE,{"disambiguationData":[TD([[makeQuery(id+"F2.imprint","INTERSECT",VERTEX,{"derivedFrom":[subQ0,sQuery(id+"F2.wireOp",EDGE,"E18.0.77.0")]}),-1.0]])],"derivedFrom":subQ0})])]}),makeQuery(id+"F9L2YdqkWQCteiL_1.opExtrude","SWEPT_FACE",FACE,{"disambiguationData":[OSD([subQ0]),TDD([makeQuery(id+"F2.imprint","IMPRINT",EDGE,{"disambiguationData":[TD([[makeQuery(id+"F2.imprint","INTERSECT",VERTEX,{"derivedFrom":[subQ0,sQuery(id+"F2.wireOp",EDGE,"E18.0.79.0")]}),-1.0]])],"derivedFrom":subQ0})])]}),makeQuery(id+"F9L2YdqkWQCteiL_1.opExtrude","SWEPT_FACE",FACE,{"disambiguationData":[OSD([subQ0]),TDD([makeQuery(id+"F2.imprint","IMPRINT",EDGE,{"disambiguationData":[TD([[makeQuery(id+"F2.imprint","INTERSECT",VERTEX,{"derivedFrom":[subQ0,sQuery(id+"F2.wireOp",EDGE,"E18.0.81.0")]}),-1.0]])],"derivedFrom":subQ0})])]}),makeQuery(id+"F9L2YdqkWQCteiL_1.opExtrude","SWEPT_FACE",FACE,{"disambiguationData":[OSD([subQ0]),TDD([makeQuery(id+"F2.imprint","IMPRINT",EDGE,{"disambiguationData":[TD([[makeQuery(id+"F2.imprint","INTERSECT",VERTEX,{"derivedFrom":[subQ0,sQuery(id+"F2.wireOp",EDGE,"E18.0.83.0")]}),-1.0]])],"derivedFrom":subQ0})])]}),makeQuery(id+"F9L2YdqkWQCteiL_1.opExtrude","SWEPT_FACE",FACE,{"disambiguationData":[OSD([subQ0]),TDD([makeQuery(id+"F2.imprint","IMPRINT",EDGE,{"disambiguationData":[TD([[makeQuery(id+"F2.imprint","INTERSECT",VERTEX,{"derivedFrom":[subQ0,sQuery(id+"F2.wireOp",EDGE,"E18.0.85.0")]}),-1.0]])],"derivedFrom":subQ0})])]}),makeQuery(id+"F9L2YdqkWQCteiL_1.opExtrude","SWEPT_FACE",FACE,{"disambiguationData":[OSD([subQ0]),TDD([makeQuery(id+"F2.imprint","IMPRINT",EDGE,{"disambiguationData":[TD([[makeQuery(id+"F2.imprint","INTERSECT",VERTEX,{"derivedFrom":[subQ0,sQuery(id+"F2.wireOp",EDGE,"E18.0.87.0")]}),-1.0]])],"derivedFrom":subQ0})])]}),makeQuery(id+"F9L2YdqkWQCteiL_1.opExtrude","SWEPT_FACE",FACE,{"disambiguationData":[OSD([subQ0]),TDD([makeQuery(id+"F2.imprint","IMPRINT",EDGE,{"disambiguationData":[TD([[makeQuery(id+"F2.imprint","INTERSECT",VERTEX,{"derivedFrom":[subQ0,sQuery(id+"F2.wireOp",EDGE,"E18.0.89.0")]}),-1.0]])],"derivedFrom":subQ0})])]}),makeQuery(id+"F9L2YdqkWQCteiL_1.opExtrude","SWEPT_FACE",FACE,{"disambiguationData":[OSD([subQ0]),TDD([makeQuery(id+"F2.imprint","IMPRINT",EDGE,{"disambiguationData":[TD([[subQ1,1.0]])],"derivedFrom":subQ0}),makeQuery(id+"F2.imprint","IMPRINT",EDGE,{"disambiguationData":[TD([[subQ1,-1.0]])],"derivedFrom":subQ0})])]})]}),makeQuery(id+"F4.opExtrude","SWEPT_FACE",FACE,{"disambiguationData":[OSD([sQuery(id+"F3.wireOp",EDGE,"E23")])]})]}),makeQuery(id+"F6.opExtrude","SWEPT_FACE",FACE,{"disambiguationData":[OSD([sQuery(id+"F5.wireOp",EDGE,"E32"),sQuery(id+"F5.wireOp",EDGE,"E33")])]})]});}
            var sketch = newSketch(context, id + "F8", { "sketchPlane" : qUnion([Q0])});
            skLineSegment(sketch, "E35", {"start": v(0, 19.05) * mm, "end": v(7.62, 19.05) * mm});
            skLineSegment(sketch, "E36", {"start": v(7.62, 19.05) * mm, "end": v(7.62, 23.01) * mm});
            skLineSegment(sketch, "E37", {"start": v(7.62, 19.05) * mm, "end": v(7.62, 21.4) * mm});
            skPoint(sketch, "E38.orphan", {"position": v(15.24, 31.45) * mm});
            skPoint(sketch, "E39.visualSharp", {"position": v(7.62, 23.01) * mm});
            skPoint(sketch, "E40.visualSharp", {"position": v(15.24, 23.01) * mm});
            skLineSegment(sketch, "E41", {"start": v(7.62, 29.21) * mm, "end": v(15.24, 29.21) * mm});
            skPoint(sketch, "E42.endSnap0", {"position": v(7.62, 24.13) * mm});
            skLineSegment(sketch, "E43", {"start": v(11.43, 29.21) * mm, "end": v(11.43, 22.94) * mm});
            skLineSegment(sketch, "E44.MirrorCS", {"start": v(15.24, 19.05) * mm, "end": v(15.24, 23.01) * mm});
            skArc(sketch, "E45", {"start": v(10.24, 29.21) * mm, "mid": v(8.3, 26.38) * mm, "end": v(7.62, 23.01) * mm});
            skArc(sketch, "E46.MirrorCS", {"start": v(12.62, 29.21) * mm, "mid": v(14.56, 26.38) * mm, "end": v(15.24, 23.01) * mm});
            skLineSegment(sketch, "E47.MirrorCS", {"start": v(15.24, 19.05) * mm, "end": v(15.24, 21.4) * mm});
            skLineSegment(sketch, "E48", {"start": v(15.24, 19.05) * mm, "end": v(7.62, 19.05) * mm});
            skLineSegment(sketch, "E49", {"start": v(12.62, 29.21) * mm, "end": v(10.24, 29.21) * mm});
            skLineSegment(sketch, "E50.1.0.0", {"start": v(27.86, 29.21) * mm, "end": v(25.48, 29.21) * mm});
            skArc(sketch, "E50.1.0.1", {"start": v(25.48, 29.21) * mm, "mid": v(23.54, 26.38) * mm, "end": v(22.86, 23.01) * mm});
            skArc(sketch, "E50.1.0.2", {"start": v(27.86, 29.21) * mm, "mid": v(29.8, 26.38) * mm, "end": v(30.48, 23.01) * mm});
            skLineSegment(sketch, "E50.1.0.3", {"start": v(30.48, 19.05) * mm, "end": v(30.48, 23.01) * mm});
            skLineSegment(sketch, "E50.1.0.4", {"start": v(22.86, 19.05) * mm, "end": v(22.86, 23.01) * mm});
            skLineSegment(sketch, "E50.1.0.5", {"start": v(30.48, 19.05) * mm, "end": v(22.86, 19.05) * mm});
            skLineSegment(sketch, "E50.2.0.0", {"start": v(43.1, 29.21) * mm, "end": v(40.72, 29.21) * mm});
            skArc(sketch, "E50.2.0.1", {"start": v(40.72, 29.21) * mm, "mid": v(38.78, 26.38) * mm, "end": v(38.1, 23.01) * mm});
            skArc(sketch, "E50.2.0.2", {"start": v(43.1, 29.21) * mm, "mid": v(45.04, 26.38) * mm, "end": v(45.72, 23.01) * mm});
            skLineSegment(sketch, "E50.2.0.3", {"start": v(45.72, 19.05) * mm, "end": v(45.72, 23.01) * mm});
            skLineSegment(sketch, "E50.2.0.4", {"start": v(38.1, 19.05) * mm, "end": v(38.1, 23.01) * mm});
            skLineSegment(sketch, "E50.2.0.5", {"start": v(45.72, 19.05) * mm, "end": v(38.1, 19.05) * mm});
            skLineSegment(sketch, "E50.3.0.0", {"start": v(58.34, 29.21) * mm, "end": v(55.96, 29.21) * mm});
            skArc(sketch, "E50.3.0.1", {"start": v(55.96, 29.21) * mm, "mid": v(54.02, 26.38) * mm, "end": v(53.34, 23.01) * mm});
            skArc(sketch, "E50.3.0.2", {"start": v(58.34, 29.21) * mm, "mid": v(60.28, 26.38) * mm, "end": v(60.96, 23.01) * mm});
            skLineSegment(sketch, "E50.3.0.3", {"start": v(60.96, 19.05) * mm, "end": v(60.96, 23.01) * mm});
            skLineSegment(sketch, "E50.3.0.4", {"start": v(53.34, 19.05) * mm, "end": v(53.34, 23.01) * mm});
            skLineSegment(sketch, "E50.3.0.5", {"start": v(60.96, 19.05) * mm, "end": v(53.34, 19.05) * mm});
            skLineSegment(sketch, "E50.4.0.0", {"start": v(73.58, 29.21) * mm, "end": v(71.2, 29.21) * mm});
            skArc(sketch, "E50.4.0.1", {"start": v(71.2, 29.21) * mm, "mid": v(69.26, 26.38) * mm, "end": v(68.58, 23.01) * mm});
            skArc(sketch, "E50.4.0.2", {"start": v(73.58, 29.21) * mm, "mid": v(75.52, 26.38) * mm, "end": v(76.2, 23.01) * mm});
            skLineSegment(sketch, "E50.4.0.3", {"start": v(76.2, 19.05) * mm, "end": v(76.2, 23.01) * mm});
            skLineSegment(sketch, "E50.4.0.4", {"start": v(68.58, 19.05) * mm, "end": v(68.58, 23.01) * mm});
            skLineSegment(sketch, "E50.4.0.5", {"start": v(76.2, 19.05) * mm, "end": v(68.58, 19.05) * mm});
            skLineSegment(sketch, "E50.5.0.0", {"start": v(88.82, 29.21) * mm, "end": v(86.44, 29.21) * mm});
            skArc(sketch, "E50.5.0.1", {"start": v(86.44, 29.21) * mm, "mid": v(84.5, 26.38) * mm, "end": v(83.82, 23.01) * mm});
            skArc(sketch, "E50.5.0.2", {"start": v(88.82, 29.21) * mm, "mid": v(90.76, 26.38) * mm, "end": v(91.44, 23.01) * mm});
            skLineSegment(sketch, "E50.5.0.3", {"start": v(91.44, 19.05) * mm, "end": v(91.44, 23.01) * mm});
            skLineSegment(sketch, "E50.5.0.4", {"start": v(83.82, 19.05) * mm, "end": v(83.82, 23.01) * mm});
            skLineSegment(sketch, "E50.5.0.5", {"start": v(91.44, 19.05) * mm, "end": v(83.82, 19.05) * mm});
            skLineSegment(sketch, "E50.6.0.0", {"start": v(104.06, 29.21) * mm, "end": v(101.68, 29.21) * mm});
            skArc(sketch, "E50.6.0.1", {"start": v(101.68, 29.21) * mm, "mid": v(99.74, 26.38) * mm, "end": v(99.06, 23.01) * mm});
            skArc(sketch, "E50.6.0.2", {"start": v(104.06, 29.21) * mm, "mid": v(106, 26.38) * mm, "end": v(106.68, 23.01) * mm});
            skLineSegment(sketch, "E50.6.0.3", {"start": v(106.68, 19.05) * mm, "end": v(106.68, 23.01) * mm});
            skLineSegment(sketch, "E50.6.0.4", {"start": v(99.06, 19.05) * mm, "end": v(99.06, 23.01) * mm});
            skLineSegment(sketch, "E50.6.0.5", {"start": v(106.68, 19.05) * mm, "end": v(99.06, 19.05) * mm});
            skLineSegment(sketch, "E50.7.0.0", {"start": v(119.3, 29.21) * mm, "end": v(116.92, 29.21) * mm});
            skArc(sketch, "E50.7.0.1", {"start": v(116.92, 29.21) * mm, "mid": v(114.98, 26.38) * mm, "end": v(114.3, 23.01) * mm});
            skArc(sketch, "E50.7.0.2", {"start": v(119.3, 29.21) * mm, "mid": v(121.24, 26.38) * mm, "end": v(121.92, 23.01) * mm});
            skLineSegment(sketch, "E50.7.0.3", {"start": v(121.92, 19.05) * mm, "end": v(121.92, 23.01) * mm});
            skLineSegment(sketch, "E50.7.0.4", {"start": v(114.3, 19.05) * mm, "end": v(114.3, 23.01) * mm});
            skLineSegment(sketch, "E50.7.0.5", {"start": v(121.92, 19.05) * mm, "end": v(114.3, 19.05) * mm});
            skLineSegment(sketch, "E50.8.0.0", {"start": v(134.54, 29.21) * mm, "end": v(132.16, 29.21) * mm});
            skArc(sketch, "E50.8.0.1", {"start": v(132.16, 29.21) * mm, "mid": v(130.22, 26.38) * mm, "end": v(129.54, 23.01) * mm});
            skArc(sketch, "E50.8.0.2", {"start": v(134.54, 29.21) * mm, "mid": v(136.48, 26.38) * mm, "end": v(137.16, 23.01) * mm});
            skLineSegment(sketch, "E50.8.0.3", {"start": v(137.16, 19.05) * mm, "end": v(137.16, 23.01) * mm});
            skLineSegment(sketch, "E50.8.0.4", {"start": v(129.54, 19.05) * mm, "end": v(129.54, 23.01) * mm});
            skLineSegment(sketch, "E50.8.0.5", {"start": v(137.16, 19.05) * mm, "end": v(129.54, 19.05) * mm});
            skLineSegment(sketch, "E50.9.0.0", {"start": v(149.78, 29.21) * mm, "end": v(147.4, 29.21) * mm});
            skArc(sketch, "E50.9.0.1", {"start": v(147.4, 29.21) * mm, "mid": v(145.46, 26.38) * mm, "end": v(144.78, 23.01) * mm});
            skArc(sketch, "E50.9.0.2", {"start": v(149.78, 29.21) * mm, "mid": v(151.72, 26.38) * mm, "end": v(152.4, 23.01) * mm});
            skLineSegment(sketch, "E50.9.0.3", {"start": v(152.4, 19.05) * mm, "end": v(152.4, 23.01) * mm});
            skLineSegment(sketch, "E50.9.0.4", {"start": v(144.78, 19.05) * mm, "end": v(144.78, 23.01) * mm});
            skLineSegment(sketch, "E50.9.0.5", {"start": v(152.4, 19.05) * mm, "end": v(144.78, 19.05) * mm});
            skLineSegment(sketch, "E50.10.0.0", {"start": v(165.02, 29.21) * mm, "end": v(162.64, 29.21) * mm});
            skArc(sketch, "E50.10.0.1", {"start": v(162.64, 29.21) * mm, "mid": v(160.7, 26.38) * mm, "end": v(160.02, 23.01) * mm});
            skArc(sketch, "E50.10.0.2", {"start": v(165.02, 29.21) * mm, "mid": v(166.96, 26.38) * mm, "end": v(167.64, 23.01) * mm});
            skLineSegment(sketch, "E50.10.0.3", {"start": v(167.64, 19.05) * mm, "end": v(167.64, 23.01) * mm});
            skLineSegment(sketch, "E50.10.0.4", {"start": v(160.02, 19.05) * mm, "end": v(160.02, 23.01) * mm});
            skLineSegment(sketch, "E50.10.0.5", {"start": v(167.64, 19.05) * mm, "end": v(160.02, 19.05) * mm});
            skLineSegment(sketch, "E50.11.0.0", {"start": v(180.26, 29.21) * mm, "end": v(177.88, 29.21) * mm});
            skArc(sketch, "E50.11.0.1", {"start": v(177.88, 29.21) * mm, "mid": v(175.94, 26.38) * mm, "end": v(175.26, 23.01) * mm});
            skArc(sketch, "E50.11.0.2", {"start": v(180.26, 29.21) * mm, "mid": v(182.2, 26.38) * mm, "end": v(182.88, 23.01) * mm});
            skLineSegment(sketch, "E50.11.0.3", {"start": v(182.88, 19.05) * mm, "end": v(182.88, 23.01) * mm});
            skLineSegment(sketch, "E50.11.0.4", {"start": v(175.26, 19.05) * mm, "end": v(175.26, 23.01) * mm});
            skLineSegment(sketch, "E50.11.0.5", {"start": v(182.88, 19.05) * mm, "end": v(175.26, 19.05) * mm});
            skLineSegment(sketch, "E50.12.0.0", {"start": v(195.5, 29.21) * mm, "end": v(193.12, 29.21) * mm});
            skArc(sketch, "E50.12.0.1", {"start": v(193.12, 29.21) * mm, "mid": v(191.18, 26.38) * mm, "end": v(190.5, 23.01) * mm});
            skArc(sketch, "E50.12.0.2", {"start": v(195.5, 29.21) * mm, "mid": v(197.44, 26.38) * mm, "end": v(198.12, 23.01) * mm});
            skLineSegment(sketch, "E50.12.0.3", {"start": v(198.12, 19.05) * mm, "end": v(198.12, 23.01) * mm});
            skLineSegment(sketch, "E50.12.0.4", {"start": v(190.5, 19.05) * mm, "end": v(190.5, 23.01) * mm});
            skLineSegment(sketch, "E50.12.0.5", {"start": v(198.12, 19.05) * mm, "end": v(190.5, 19.05) * mm});
            skLineSegment(sketch, "E50.13.0.0", {"start": v(210.74, 29.21) * mm, "end": v(208.36, 29.21) * mm});
            skArc(sketch, "E50.13.0.1", {"start": v(208.36, 29.21) * mm, "mid": v(206.42, 26.38) * mm, "end": v(205.74, 23.01) * mm});
            skArc(sketch, "E50.13.0.2", {"start": v(210.74, 29.21) * mm, "mid": v(212.68, 26.38) * mm, "end": v(213.36, 23.01) * mm});
            skLineSegment(sketch, "E50.13.0.3", {"start": v(213.36, 19.05) * mm, "end": v(213.36, 23.01) * mm});
            skLineSegment(sketch, "E50.13.0.4", {"start": v(205.74, 19.05) * mm, "end": v(205.74, 23.01) * mm});
            skLineSegment(sketch, "E50.13.0.5", {"start": v(213.36, 19.05) * mm, "end": v(205.74, 19.05) * mm});
            skLineSegment(sketch, "E50.14.0.0", {"start": v(225.98, 29.21) * mm, "end": v(223.6, 29.21) * mm});
            skArc(sketch, "E50.14.0.1", {"start": v(223.6, 29.21) * mm, "mid": v(221.66, 26.38) * mm, "end": v(220.98, 23.01) * mm});
            skArc(sketch, "E50.14.0.2", {"start": v(225.98, 29.21) * mm, "mid": v(227.92, 26.38) * mm, "end": v(228.6, 23.01) * mm});
            skLineSegment(sketch, "E50.14.0.3", {"start": v(228.6, 19.05) * mm, "end": v(228.6, 23.01) * mm});
            skLineSegment(sketch, "E50.14.0.4", {"start": v(220.98, 19.05) * mm, "end": v(220.98, 23.01) * mm});
            skLineSegment(sketch, "E50.14.0.5", {"start": v(228.6, 19.05) * mm, "end": v(220.98, 19.05) * mm});
            skLineSegment(sketch, "E50.15.0.0", {"start": v(241.22, 29.21) * mm, "end": v(238.84, 29.21) * mm});
            skArc(sketch, "E50.15.0.1", {"start": v(238.84, 29.21) * mm, "mid": v(236.9, 26.38) * mm, "end": v(236.22, 23.01) * mm});
            skArc(sketch, "E50.15.0.2", {"start": v(241.22, 29.21) * mm, "mid": v(243.16, 26.38) * mm, "end": v(243.84, 23.01) * mm});
            skLineSegment(sketch, "E50.15.0.3", {"start": v(243.84, 19.05) * mm, "end": v(243.84, 23.01) * mm});
            skLineSegment(sketch, "E50.15.0.4", {"start": v(236.22, 19.05) * mm, "end": v(236.22, 23.01) * mm});
            skLineSegment(sketch, "E50.15.0.5", {"start": v(243.84, 19.05) * mm, "end": v(236.22, 19.05) * mm});
            skLineSegment(sketch, "E50.16.0.0", {"start": v(256.46, 29.21) * mm, "end": v(254.08, 29.21) * mm});
            skArc(sketch, "E50.16.0.1", {"start": v(254.08, 29.21) * mm, "mid": v(252.14, 26.38) * mm, "end": v(251.46, 23.01) * mm});
            skArc(sketch, "E50.16.0.2", {"start": v(256.46, 29.21) * mm, "mid": v(258.4, 26.38) * mm, "end": v(259.08, 23.01) * mm});
            skLineSegment(sketch, "E50.16.0.3", {"start": v(259.08, 19.05) * mm, "end": v(259.08, 23.01) * mm});
            skLineSegment(sketch, "E50.16.0.4", {"start": v(251.46, 19.05) * mm, "end": v(251.46, 23.01) * mm});
            skLineSegment(sketch, "E50.16.0.5", {"start": v(259.08, 19.05) * mm, "end": v(251.46, 19.05) * mm});
            skLineSegment(sketch, "E50.17.0.0", {"start": v(271.7, 29.21) * mm, "end": v(269.32, 29.21) * mm});
            skArc(sketch, "E50.17.0.1", {"start": v(269.32, 29.21) * mm, "mid": v(267.38, 26.38) * mm, "end": v(266.7, 23.01) * mm});
            skArc(sketch, "E50.17.0.2", {"start": v(271.7, 29.21) * mm, "mid": v(273.64, 26.38) * mm, "end": v(274.32, 23.01) * mm});
            skLineSegment(sketch, "E50.17.0.3", {"start": v(274.32, 19.05) * mm, "end": v(274.32, 23.01) * mm});
            skLineSegment(sketch, "E50.17.0.4", {"start": v(266.7, 19.05) * mm, "end": v(266.7, 23.01) * mm});
            skLineSegment(sketch, "E50.17.0.5", {"start": v(274.32, 19.05) * mm, "end": v(266.7, 19.05) * mm});
            skLineSegment(sketch, "E50.18.0.0", {"start": v(286.94, 29.21) * mm, "end": v(284.56, 29.21) * mm});
            skArc(sketch, "E50.18.0.1", {"start": v(284.56, 29.21) * mm, "mid": v(282.62, 26.38) * mm, "end": v(281.94, 23.01) * mm});
            skArc(sketch, "E50.18.0.2", {"start": v(286.94, 29.21) * mm, "mid": v(288.88, 26.38) * mm, "end": v(289.56, 23.01) * mm});
            skLineSegment(sketch, "E50.18.0.3", {"start": v(289.56, 19.05) * mm, "end": v(289.56, 23.01) * mm});
            skLineSegment(sketch, "E50.18.0.4", {"start": v(281.94, 19.05) * mm, "end": v(281.94, 23.01) * mm});
            skLineSegment(sketch, "E50.18.0.5", {"start": v(289.56, 19.05) * mm, "end": v(281.94, 19.05) * mm});
            skLineSegment(sketch, "E50.19.0.0", {"start": v(302.18, 29.21) * mm, "end": v(299.8, 29.21) * mm});
            skArc(sketch, "E50.19.0.1", {"start": v(299.8, 29.21) * mm, "mid": v(297.86, 26.38) * mm, "end": v(297.18, 23.01) * mm});
            skArc(sketch, "E50.19.0.2", {"start": v(302.18, 29.21) * mm, "mid": v(304.12, 26.38) * mm, "end": v(304.8, 23.01) * mm});
            skLineSegment(sketch, "E50.19.0.3", {"start": v(304.8, 19.05) * mm, "end": v(304.8, 23.01) * mm});
            skLineSegment(sketch, "E50.19.0.4", {"start": v(297.18, 19.05) * mm, "end": v(297.18, 23.01) * mm});
            skLineSegment(sketch, "E50.19.0.5", {"start": v(304.8, 19.05) * mm, "end": v(297.18, 19.05) * mm});
            skLineSegment(sketch, "E50.20.0.0", {"start": v(317.42, 29.21) * mm, "end": v(315.04, 29.21) * mm});
            skArc(sketch, "E50.20.0.1", {"start": v(315.04, 29.21) * mm, "mid": v(313.1, 26.38) * mm, "end": v(312.42, 23.01) * mm});
            skArc(sketch, "E50.20.0.2", {"start": v(317.42, 29.21) * mm, "mid": v(319.36, 26.38) * mm, "end": v(320.04, 23.01) * mm});
            skLineSegment(sketch, "E50.20.0.3", {"start": v(320.04, 19.05) * mm, "end": v(320.04, 23.01) * mm});
            skLineSegment(sketch, "E50.20.0.4", {"start": v(312.42, 19.05) * mm, "end": v(312.42, 23.01) * mm});
            skLineSegment(sketch, "E50.20.0.5", {"start": v(320.04, 19.05) * mm, "end": v(312.42, 19.05) * mm});
            skLineSegment(sketch, "E50.21.0.0", {"start": v(332.66, 29.21) * mm, "end": v(330.28, 29.21) * mm});
            skArc(sketch, "E50.21.0.1", {"start": v(330.28, 29.21) * mm, "mid": v(328.34, 26.38) * mm, "end": v(327.66, 23.01) * mm});
            skArc(sketch, "E50.21.0.2", {"start": v(332.66, 29.21) * mm, "mid": v(334.6, 26.38) * mm, "end": v(335.28, 23.01) * mm});
            skLineSegment(sketch, "E50.21.0.3", {"start": v(335.28, 19.05) * mm, "end": v(335.28, 23.01) * mm});
            skLineSegment(sketch, "E50.21.0.4", {"start": v(327.66, 19.05) * mm, "end": v(327.66, 23.01) * mm});
            skLineSegment(sketch, "E50.21.0.5", {"start": v(335.28, 19.05) * mm, "end": v(327.66, 19.05) * mm});
            skLineSegment(sketch, "E50.22.0.0", {"start": v(347.9, 29.21) * mm, "end": v(345.52, 29.21) * mm});
            skArc(sketch, "E50.22.0.1", {"start": v(345.52, 29.21) * mm, "mid": v(343.58, 26.38) * mm, "end": v(342.9, 23.01) * mm});
            skArc(sketch, "E50.22.0.2", {"start": v(347.9, 29.21) * mm, "mid": v(349.84, 26.38) * mm, "end": v(350.52, 23.01) * mm});
            skLineSegment(sketch, "E50.22.0.3", {"start": v(350.52, 19.05) * mm, "end": v(350.52, 23.01) * mm});
            skLineSegment(sketch, "E50.22.0.4", {"start": v(342.9, 19.05) * mm, "end": v(342.9, 23.01) * mm});
            skLineSegment(sketch, "E50.22.0.5", {"start": v(350.52, 19.05) * mm, "end": v(342.9, 19.05) * mm});
            skLineSegment(sketch, "E50.23.0.0", {"start": v(363.14, 29.21) * mm, "end": v(360.76, 29.21) * mm});
            skArc(sketch, "E50.23.0.1", {"start": v(360.76, 29.21) * mm, "mid": v(358.82, 26.38) * mm, "end": v(358.14, 23.01) * mm});
            skArc(sketch, "E50.23.0.2", {"start": v(363.14, 29.21) * mm, "mid": v(365.08, 26.38) * mm, "end": v(365.76, 23.01) * mm});
            skLineSegment(sketch, "E50.23.0.3", {"start": v(365.76, 19.05) * mm, "end": v(365.76, 23.01) * mm});
            skLineSegment(sketch, "E50.23.0.4", {"start": v(358.14, 19.05) * mm, "end": v(358.14, 23.01) * mm});
            skLineSegment(sketch, "E50.23.0.5", {"start": v(365.76, 19.05) * mm, "end": v(358.14, 19.05) * mm});
            skLineSegment(sketch, "E50.24.0.0", {"start": v(378.38, 29.21) * mm, "end": v(376, 29.21) * mm});
            skArc(sketch, "E50.24.0.1", {"start": v(376, 29.21) * mm, "mid": v(374.06, 26.38) * mm, "end": v(373.38, 23.01) * mm});
            skArc(sketch, "E50.24.0.2", {"start": v(378.38, 29.21) * mm, "mid": v(380.32, 26.38) * mm, "end": v(381, 23.01) * mm});
            skLineSegment(sketch, "E50.24.0.3", {"start": v(381, 19.05) * mm, "end": v(381, 23.01) * mm});
            skLineSegment(sketch, "E50.24.0.4", {"start": v(373.38, 19.05) * mm, "end": v(373.38, 23.01) * mm});
            skLineSegment(sketch, "E50.24.0.5", {"start": v(381, 19.05) * mm, "end": v(373.38, 19.05) * mm});
            skLineSegment(sketch, "E50.25.0.0", {"start": v(393.62, 29.21) * mm, "end": v(391.24, 29.21) * mm});
            skArc(sketch, "E50.25.0.1", {"start": v(391.24, 29.21) * mm, "mid": v(389.3, 26.38) * mm, "end": v(388.62, 23.01) * mm});
            skArc(sketch, "E50.25.0.2", {"start": v(393.62, 29.21) * mm, "mid": v(395.56, 26.38) * mm, "end": v(396.24, 23.01) * mm});
            skLineSegment(sketch, "E50.25.0.3", {"start": v(396.24, 19.05) * mm, "end": v(396.24, 23.01) * mm});
            skLineSegment(sketch, "E50.25.0.4", {"start": v(388.62, 19.05) * mm, "end": v(388.62, 23.01) * mm});
            skLineSegment(sketch, "E50.25.0.5", {"start": v(396.24, 19.05) * mm, "end": v(388.62, 19.05) * mm});
            skLineSegment(sketch, "E50.26.0.0", {"start": v(408.86, 29.21) * mm, "end": v(406.48, 29.21) * mm});
            skArc(sketch, "E50.26.0.1", {"start": v(406.48, 29.21) * mm, "mid": v(404.54, 26.38) * mm, "end": v(403.86, 23.01) * mm});
            skArc(sketch, "E50.26.0.2", {"start": v(408.86, 29.21) * mm, "mid": v(410.8, 26.38) * mm, "end": v(411.48, 23.01) * mm});
            skLineSegment(sketch, "E50.26.0.3", {"start": v(411.48, 19.05) * mm, "end": v(411.48, 23.01) * mm});
            skLineSegment(sketch, "E50.26.0.4", {"start": v(403.86, 19.05) * mm, "end": v(403.86, 23.01) * mm});
            skLineSegment(sketch, "E50.26.0.5", {"start": v(411.48, 19.05) * mm, "end": v(403.86, 19.05) * mm});
            skLineSegment(sketch, "E50.27.0.0", {"start": v(424.1, 29.21) * mm, "end": v(421.72, 29.21) * mm});
            skArc(sketch, "E50.27.0.1", {"start": v(421.72, 29.21) * mm, "mid": v(419.78, 26.38) * mm, "end": v(419.1, 23.01) * mm});
            skArc(sketch, "E50.27.0.2", {"start": v(424.1, 29.21) * mm, "mid": v(426.04, 26.38) * mm, "end": v(426.72, 23.01) * mm});
            skLineSegment(sketch, "E50.27.0.3", {"start": v(426.72, 19.05) * mm, "end": v(426.72, 23.01) * mm});
            skLineSegment(sketch, "E50.27.0.4", {"start": v(419.1, 19.05) * mm, "end": v(419.1, 23.01) * mm});
            skLineSegment(sketch, "E50.27.0.5", {"start": v(426.72, 19.05) * mm, "end": v(419.1, 19.05) * mm});
            skLineSegment(sketch, "E50.28.0.0", {"start": v(439.34, 29.21) * mm, "end": v(436.96, 29.21) * mm});
            skArc(sketch, "E50.28.0.1", {"start": v(436.96, 29.21) * mm, "mid": v(435.02, 26.38) * mm, "end": v(434.34, 23.01) * mm});
            skArc(sketch, "E50.28.0.2", {"start": v(439.34, 29.21) * mm, "mid": v(441.28, 26.38) * mm, "end": v(441.96, 23.01) * mm});
            skLineSegment(sketch, "E50.28.0.3", {"start": v(441.96, 19.05) * mm, "end": v(441.96, 23.01) * mm});
            skLineSegment(sketch, "E50.28.0.4", {"start": v(434.34, 19.05) * mm, "end": v(434.34, 23.01) * mm});
            skLineSegment(sketch, "E50.28.0.5", {"start": v(441.96, 19.05) * mm, "end": v(434.34, 19.05) * mm});
            skLineSegment(sketch, "E50.29.0.0", {"start": v(454.58, 29.21) * mm, "end": v(452.2, 29.21) * mm});
            skArc(sketch, "E50.29.0.1", {"start": v(452.2, 29.21) * mm, "mid": v(450.26, 26.38) * mm, "end": v(449.58, 23.01) * mm});
            skArc(sketch, "E50.29.0.2", {"start": v(454.58, 29.21) * mm, "mid": v(456.52, 26.38) * mm, "end": v(457.2, 23.01) * mm});
            skLineSegment(sketch, "E50.29.0.3", {"start": v(457.2, 19.05) * mm, "end": v(457.2, 23.01) * mm});
            skLineSegment(sketch, "E50.29.0.4", {"start": v(449.58, 19.05) * mm, "end": v(449.58, 23.01) * mm});
            skLineSegment(sketch, "E50.29.0.5", {"start": v(457.2, 19.05) * mm, "end": v(449.58, 19.05) * mm});
            skLineSegment(sketch, "E50.30.0.0", {"start": v(469.82, 29.21) * mm, "end": v(467.44, 29.21) * mm});
            skArc(sketch, "E50.30.0.1", {"start": v(467.44, 29.21) * mm, "mid": v(465.5, 26.38) * mm, "end": v(464.82, 23.01) * mm});
            skArc(sketch, "E50.30.0.2", {"start": v(469.82, 29.21) * mm, "mid": v(471.76, 26.38) * mm, "end": v(472.44, 23.01) * mm});
            skLineSegment(sketch, "E50.30.0.3", {"start": v(472.44, 19.05) * mm, "end": v(472.44, 23.01) * mm});
            skLineSegment(sketch, "E50.30.0.4", {"start": v(464.82, 19.05) * mm, "end": v(464.82, 23.01) * mm});
            skLineSegment(sketch, "E50.30.0.5", {"start": v(472.44, 19.05) * mm, "end": v(464.82, 19.05) * mm});
            skLineSegment(sketch, "E50.31.0.0", {"start": v(485.06, 29.21) * mm, "end": v(482.68, 29.21) * mm});
            skArc(sketch, "E50.31.0.1", {"start": v(482.68, 29.21) * mm, "mid": v(480.74, 26.38) * mm, "end": v(480.06, 23.01) * mm});
            skArc(sketch, "E50.31.0.2", {"start": v(485.06, 29.21) * mm, "mid": v(487, 26.38) * mm, "end": v(487.68, 23.01) * mm});
            skLineSegment(sketch, "E50.31.0.3", {"start": v(487.68, 19.05) * mm, "end": v(487.68, 23.01) * mm});
            skLineSegment(sketch, "E50.31.0.4", {"start": v(480.06, 19.05) * mm, "end": v(480.06, 23.01) * mm});
            skLineSegment(sketch, "E50.31.0.5", {"start": v(487.68, 19.05) * mm, "end": v(480.06, 19.05) * mm});
            skLineSegment(sketch, "E50.32.0.0", {"start": v(500.3, 29.21) * mm, "end": v(497.92, 29.21) * mm});
            skArc(sketch, "E50.32.0.1", {"start": v(497.92, 29.21) * mm, "mid": v(495.98, 26.38) * mm, "end": v(495.3, 23.01) * mm});
            skArc(sketch, "E50.32.0.2", {"start": v(500.3, 29.2) * mm, "mid": v(502.24, 26.38) * mm, "end": v(502.92, 23.01) * mm});
            skLineSegment(sketch, "E50.32.0.3", {"start": v(502.92, 19.05) * mm, "end": v(502.92, 23.01) * mm});
            skLineSegment(sketch, "E50.32.0.4", {"start": v(495.3, 19.05) * mm, "end": v(495.3, 23.01) * mm});
            skLineSegment(sketch, "E50.32.0.5", {"start": v(502.92, 19.05) * mm, "end": v(495.3, 19.05) * mm});
            skLineSegment(sketch, "E50.33.0.0", {"start": v(515.54, 29.21) * mm, "end": v(513.16, 29.21) * mm});
            skArc(sketch, "E50.33.0.1", {"start": v(513.16, 29.21) * mm, "mid": v(511.22, 26.38) * mm, "end": v(510.54, 23.01) * mm});
            skArc(sketch, "E50.33.0.2", {"start": v(515.54, 29.21) * mm, "mid": v(517.48, 26.38) * mm, "end": v(518.16, 23.01) * mm});
            skLineSegment(sketch, "E50.33.0.3", {"start": v(518.16, 19.05) * mm, "end": v(518.16, 23.01) * mm});
            skLineSegment(sketch, "E50.33.0.4", {"start": v(510.54, 19.05) * mm, "end": v(510.54, 23.01) * mm});
            skLineSegment(sketch, "E50.33.0.5", {"start": v(518.16, 19.05) * mm, "end": v(510.54, 19.05) * mm});
            skLineSegment(sketch, "E50.34.0.0", {"start": v(530.78, 29.21) * mm, "end": v(528.4, 29.21) * mm});
            skArc(sketch, "E50.34.0.1", {"start": v(528.4, 29.21) * mm, "mid": v(526.46, 26.38) * mm, "end": v(525.78, 23.01) * mm});
            skArc(sketch, "E50.34.0.2", {"start": v(530.78, 29.21) * mm, "mid": v(532.72, 26.38) * mm, "end": v(533.4, 23.01) * mm});
            skLineSegment(sketch, "E50.34.0.3", {"start": v(533.4, 19.05) * mm, "end": v(533.4, 23.01) * mm});
            skLineSegment(sketch, "E50.34.0.4", {"start": v(525.78, 19.05) * mm, "end": v(525.78, 23.01) * mm});
            skLineSegment(sketch, "E50.34.0.5", {"start": v(533.4, 19.05) * mm, "end": v(525.78, 19.05) * mm});
            skLineSegment(sketch, "E50.35.0.0", {"start": v(546.02, 29.21) * mm, "end": v(543.64, 29.21) * mm});
            skArc(sketch, "E50.35.0.1", {"start": v(543.64, 29.21) * mm, "mid": v(541.7, 26.38) * mm, "end": v(541.02, 23.01) * mm});
            skArc(sketch, "E50.35.0.2", {"start": v(546.02, 29.21) * mm, "mid": v(547.96, 26.38) * mm, "end": v(548.64, 23.01) * mm});
            skLineSegment(sketch, "E50.35.0.3", {"start": v(548.64, 19.05) * mm, "end": v(548.64, 23.01) * mm});
            skLineSegment(sketch, "E50.35.0.4", {"start": v(541.02, 19.05) * mm, "end": v(541.02, 23.01) * mm});
            skLineSegment(sketch, "E50.35.0.5", {"start": v(548.64, 19.05) * mm, "end": v(541.02, 19.05) * mm});
            skLineSegment(sketch, "E50.36.0.0", {"start": v(561.26, 29.21) * mm, "end": v(558.88, 29.21) * mm});
            skArc(sketch, "E50.36.0.1", {"start": v(558.88, 29.21) * mm, "mid": v(556.94, 26.38) * mm, "end": v(556.26, 23.01) * mm});
            skArc(sketch, "E50.36.0.2", {"start": v(561.26, 29.21) * mm, "mid": v(563.2, 26.38) * mm, "end": v(563.88, 23.01) * mm});
            skLineSegment(sketch, "E50.36.0.3", {"start": v(563.88, 19.05) * mm, "end": v(563.88, 23.01) * mm});
            skLineSegment(sketch, "E50.36.0.4", {"start": v(556.26, 19.05) * mm, "end": v(556.26, 23.01) * mm});
            skLineSegment(sketch, "E50.36.0.5", {"start": v(563.88, 19.05) * mm, "end": v(556.26, 19.05) * mm});
            skLineSegment(sketch, "E50.37.0.0", {"start": v(576.5, 29.21) * mm, "end": v(574.12, 29.21) * mm});
            skArc(sketch, "E50.37.0.1", {"start": v(574.12, 29.21) * mm, "mid": v(572.18, 26.38) * mm, "end": v(571.5, 23.01) * mm});
            skArc(sketch, "E50.37.0.2", {"start": v(576.5, 29.21) * mm, "mid": v(578.44, 26.38) * mm, "end": v(579.12, 23.01) * mm});
            skLineSegment(sketch, "E50.37.0.3", {"start": v(579.12, 19.05) * mm, "end": v(579.12, 23.01) * mm});
            skLineSegment(sketch, "E50.37.0.4", {"start": v(571.5, 19.05) * mm, "end": v(571.5, 23.01) * mm});
            skLineSegment(sketch, "E50.37.0.5", {"start": v(579.12, 19.05) * mm, "end": v(571.5, 19.05) * mm});
            skLineSegment(sketch, "E50.38.0.0", {"start": v(591.74, 29.21) * mm, "end": v(589.36, 29.21) * mm});
            skArc(sketch, "E50.38.0.1", {"start": v(589.36, 29.21) * mm, "mid": v(587.42, 26.38) * mm, "end": v(586.74, 23.01) * mm});
            skArc(sketch, "E50.38.0.2", {"start": v(591.74, 29.21) * mm, "mid": v(593.68, 26.38) * mm, "end": v(594.36, 23.01) * mm});
            skLineSegment(sketch, "E50.38.0.3", {"start": v(594.36, 19.05) * mm, "end": v(594.36, 23.01) * mm});
            skLineSegment(sketch, "E50.38.0.4", {"start": v(586.74, 19.05) * mm, "end": v(586.74, 23.01) * mm});
            skLineSegment(sketch, "E50.38.0.5", {"start": v(594.36, 19.05) * mm, "end": v(586.74, 19.05) * mm});
            skLineSegment(sketch, "E50.39.0.0", {"start": v(606.98, 29.21) * mm, "end": v(604.6, 29.21) * mm});
            skArc(sketch, "E50.39.0.1", {"start": v(604.6, 29.21) * mm, "mid": v(602.66, 26.38) * mm, "end": v(601.98, 23.01) * mm});
            skArc(sketch, "E50.39.0.2", {"start": v(606.98, 29.21) * mm, "mid": v(608.92, 26.38) * mm, "end": v(609.6, 23.01) * mm});
            skLineSegment(sketch, "E50.39.0.3", {"start": v(609.6, 19.05) * mm, "end": v(609.6, 23.01) * mm});
            skLineSegment(sketch, "E50.39.0.4", {"start": v(601.98, 19.05) * mm, "end": v(601.98, 23.01) * mm});
            skLineSegment(sketch, "E50.39.0.5", {"start": v(609.6, 19.05) * mm, "end": v(601.98, 19.05) * mm});
            skLineSegment(sketch, "E50.40.0.0", {"start": v(622.22, 29.21) * mm, "end": v(619.84, 29.21) * mm});
            skArc(sketch, "E50.40.0.1", {"start": v(619.84, 29.21) * mm, "mid": v(617.9, 26.38) * mm, "end": v(617.22, 23.01) * mm});
            skArc(sketch, "E50.40.0.2", {"start": v(622.22, 29.21) * mm, "mid": v(624.16, 26.38) * mm, "end": v(624.84, 23.01) * mm});
            skLineSegment(sketch, "E50.40.0.3", {"start": v(624.84, 19.05) * mm, "end": v(624.84, 23.01) * mm});
            skLineSegment(sketch, "E50.40.0.4", {"start": v(617.22, 19.05) * mm, "end": v(617.22, 23.01) * mm});
            skLineSegment(sketch, "E50.40.0.5", {"start": v(624.84, 19.05) * mm, "end": v(617.22, 19.05) * mm});
            skLineSegment(sketch, "E50.41.0.0", {"start": v(637.46, 29.21) * mm, "end": v(635.08, 29.21) * mm});
            skArc(sketch, "E50.41.0.1", {"start": v(635.08, 29.21) * mm, "mid": v(633.14, 26.38) * mm, "end": v(632.46, 23.01) * mm});
            skArc(sketch, "E50.41.0.2", {"start": v(637.46, 29.21) * mm, "mid": v(639.4, 26.38) * mm, "end": v(640.08, 23.01) * mm});
            skLineSegment(sketch, "E50.41.0.3", {"start": v(640.08, 19.05) * mm, "end": v(640.08, 23.01) * mm});
            skLineSegment(sketch, "E50.41.0.4", {"start": v(632.46, 19.05) * mm, "end": v(632.46, 23.01) * mm});
            skLineSegment(sketch, "E50.41.0.5", {"start": v(640.08, 19.05) * mm, "end": v(632.46, 19.05) * mm});
            skLineSegment(sketch, "E50.42.0.0", {"start": v(652.7, 29.21) * mm, "end": v(650.32, 29.21) * mm});
            skArc(sketch, "E50.42.0.1", {"start": v(650.32, 29.21) * mm, "mid": v(648.38, 26.38) * mm, "end": v(647.7, 23.01) * mm});
            skArc(sketch, "E50.42.0.2", {"start": v(652.7, 29.21) * mm, "mid": v(654.64, 26.38) * mm, "end": v(655.32, 23.01) * mm});
            skLineSegment(sketch, "E50.42.0.3", {"start": v(655.32, 19.05) * mm, "end": v(655.32, 23.01) * mm});
            skLineSegment(sketch, "E50.42.0.4", {"start": v(647.7, 19.05) * mm, "end": v(647.7, 23.01) * mm});
            skLineSegment(sketch, "E50.42.0.5", {"start": v(655.32, 19.05) * mm, "end": v(647.7, 19.05) * mm});
            skLineSegment(sketch, "E50.43.0.0", {"start": v(667.94, 29.21) * mm, "end": v(665.56, 29.21) * mm});
            skArc(sketch, "E50.43.0.1", {"start": v(665.56, 29.21) * mm, "mid": v(663.62, 26.38) * mm, "end": v(662.94, 23.01) * mm});
            skArc(sketch, "E50.43.0.2", {"start": v(667.94, 29.21) * mm, "mid": v(669.88, 26.38) * mm, "end": v(670.56, 23.01) * mm});
            skLineSegment(sketch, "E50.43.0.3", {"start": v(670.56, 19.05) * mm, "end": v(670.56, 23.01) * mm});
            skLineSegment(sketch, "E50.43.0.4", {"start": v(662.94, 19.05) * mm, "end": v(662.94, 23.01) * mm});
            skLineSegment(sketch, "E50.43.0.5", {"start": v(670.56, 19.05) * mm, "end": v(662.94, 19.05) * mm});
            skLineSegment(sketch, "E50.44.0.0", {"start": v(683.18, 29.21) * mm, "end": v(680.8, 29.21) * mm});
            skArc(sketch, "E50.44.0.1", {"start": v(680.8, 29.21) * mm, "mid": v(678.86, 26.38) * mm, "end": v(678.18, 23.01) * mm});
            skArc(sketch, "E50.44.0.2", {"start": v(683.18, 29.21) * mm, "mid": v(685.12, 26.38) * mm, "end": v(685.8, 23.01) * mm});
            skLineSegment(sketch, "E50.44.0.3", {"start": v(685.8, 19.05) * mm, "end": v(685.8, 23.01) * mm});
            skLineSegment(sketch, "E50.44.0.4", {"start": v(678.18, 19.05) * mm, "end": v(678.18, 23.01) * mm});
            skLineSegment(sketch, "E50.44.0.5", {"start": v(685.8, 19.05) * mm, "end": v(678.18, 19.05) * mm});
            skLineSegment(sketch, "E50.45.0.0", {"start": v(698.42, 29.21) * mm, "end": v(696.04, 29.21) * mm});
            skArc(sketch, "E50.45.0.1", {"start": v(696.04, 29.21) * mm, "mid": v(694.1, 26.38) * mm, "end": v(693.42, 23.01) * mm});
            skArc(sketch, "E50.45.0.2", {"start": v(698.42, 29.21) * mm, "mid": v(700.36, 26.38) * mm, "end": v(701.04, 23.01) * mm});
            skLineSegment(sketch, "E50.45.0.3", {"start": v(701.04, 19.05) * mm, "end": v(701.04, 23.01) * mm});
            skLineSegment(sketch, "E50.45.0.4", {"start": v(693.42, 19.05) * mm, "end": v(693.42, 23.01) * mm});
            skLineSegment(sketch, "E50.45.0.5", {"start": v(701.04, 19.05) * mm, "end": v(693.42, 19.05) * mm});
            skLineSegment(sketch, "E50.46.0.0", {"start": v(713.66, 29.21) * mm, "end": v(711.28, 29.21) * mm});
            skArc(sketch, "E50.46.0.1", {"start": v(711.28, 29.21) * mm, "mid": v(709.34, 26.38) * mm, "end": v(708.66, 23.01) * mm});
            skArc(sketch, "E50.46.0.2", {"start": v(713.66, 29.21) * mm, "mid": v(715.6, 26.38) * mm, "end": v(716.28, 23.01) * mm});
            skLineSegment(sketch, "E50.46.0.3", {"start": v(716.28, 19.05) * mm, "end": v(716.28, 23.01) * mm});
            skLineSegment(sketch, "E50.46.0.4", {"start": v(708.66, 19.05) * mm, "end": v(708.66, 23.01) * mm});
            skLineSegment(sketch, "E50.46.0.5", {"start": v(716.28, 19.05) * mm, "end": v(708.66, 19.05) * mm});
            skLineSegment(sketch, "E50.47.0.0", {"start": v(728.9, 29.21) * mm, "end": v(726.52, 29.21) * mm});
            skArc(sketch, "E50.47.0.1", {"start": v(726.52, 29.21) * mm, "mid": v(724.58, 26.38) * mm, "end": v(723.9, 23.01) * mm});
            skArc(sketch, "E50.47.0.2", {"start": v(728.9, 29.21) * mm, "mid": v(730.84, 26.38) * mm, "end": v(731.52, 23.01) * mm});
            skLineSegment(sketch, "E50.47.0.3", {"start": v(731.52, 19.05) * mm, "end": v(731.52, 23.01) * mm});
            skLineSegment(sketch, "E50.47.0.4", {"start": v(723.9, 19.05) * mm, "end": v(723.9, 23.01) * mm});
            skLineSegment(sketch, "E50.47.0.5", {"start": v(731.52, 19.05) * mm, "end": v(723.9, 19.05) * mm});
            skLineSegment(sketch, "E50.48.0.0", {"start": v(744.14, 29.21) * mm, "end": v(741.76, 29.21) * mm});
            skArc(sketch, "E50.48.0.1", {"start": v(741.76, 29.21) * mm, "mid": v(739.82, 26.38) * mm, "end": v(739.14, 23.01) * mm});
            skArc(sketch, "E50.48.0.2", {"start": v(744.14, 29.21) * mm, "mid": v(746.08, 26.38) * mm, "end": v(746.76, 23.01) * mm});
            skLineSegment(sketch, "E50.48.0.3", {"start": v(746.76, 19.05) * mm, "end": v(746.76, 23.01) * mm});
            skLineSegment(sketch, "E50.48.0.4", {"start": v(739.14, 19.05) * mm, "end": v(739.14, 23.01) * mm});
            skLineSegment(sketch, "E50.48.0.5", {"start": v(746.76, 19.05) * mm, "end": v(739.14, 19.05) * mm});
            skLineSegment(sketch, "E50.49.0.0", {"start": v(759.38, 29.21) * mm, "end": v(757, 29.21) * mm});
            skArc(sketch, "E50.49.0.1", {"start": v(757, 29.21) * mm, "mid": v(755.06, 26.38) * mm, "end": v(754.38, 23.01) * mm});
            skArc(sketch, "E50.49.0.2", {"start": v(759.38, 29.21) * mm, "mid": v(761.32, 26.38) * mm, "end": v(762, 23.01) * mm});
            skLineSegment(sketch, "E50.49.0.3", {"start": v(762, 19.05) * mm, "end": v(762, 23.01) * mm});
            skLineSegment(sketch, "E50.49.0.4", {"start": v(754.38, 19.05) * mm, "end": v(754.38, 23.01) * mm});
            skLineSegment(sketch, "E50.49.0.5", {"start": v(762, 19.05) * mm, "end": v(754.38, 19.05) * mm});
            skLineSegment(sketch, "E50.direction1", {"start": v(10.24, 29.21) * mm, "end": v(25.48, 29.21) * mm, "construction": true});
            skSolve(sketch);
        }
        {
            var Q0;
            Q0 = qSketchRegion(id + "F8", true);
            extrude(context, id + "F9", {"entities" : qUnion([Q0]), "operationType" : NewBodyOperationType.ADD, "oppositeDirection" : true, "depth" : 127 * mm});
        }
    });
